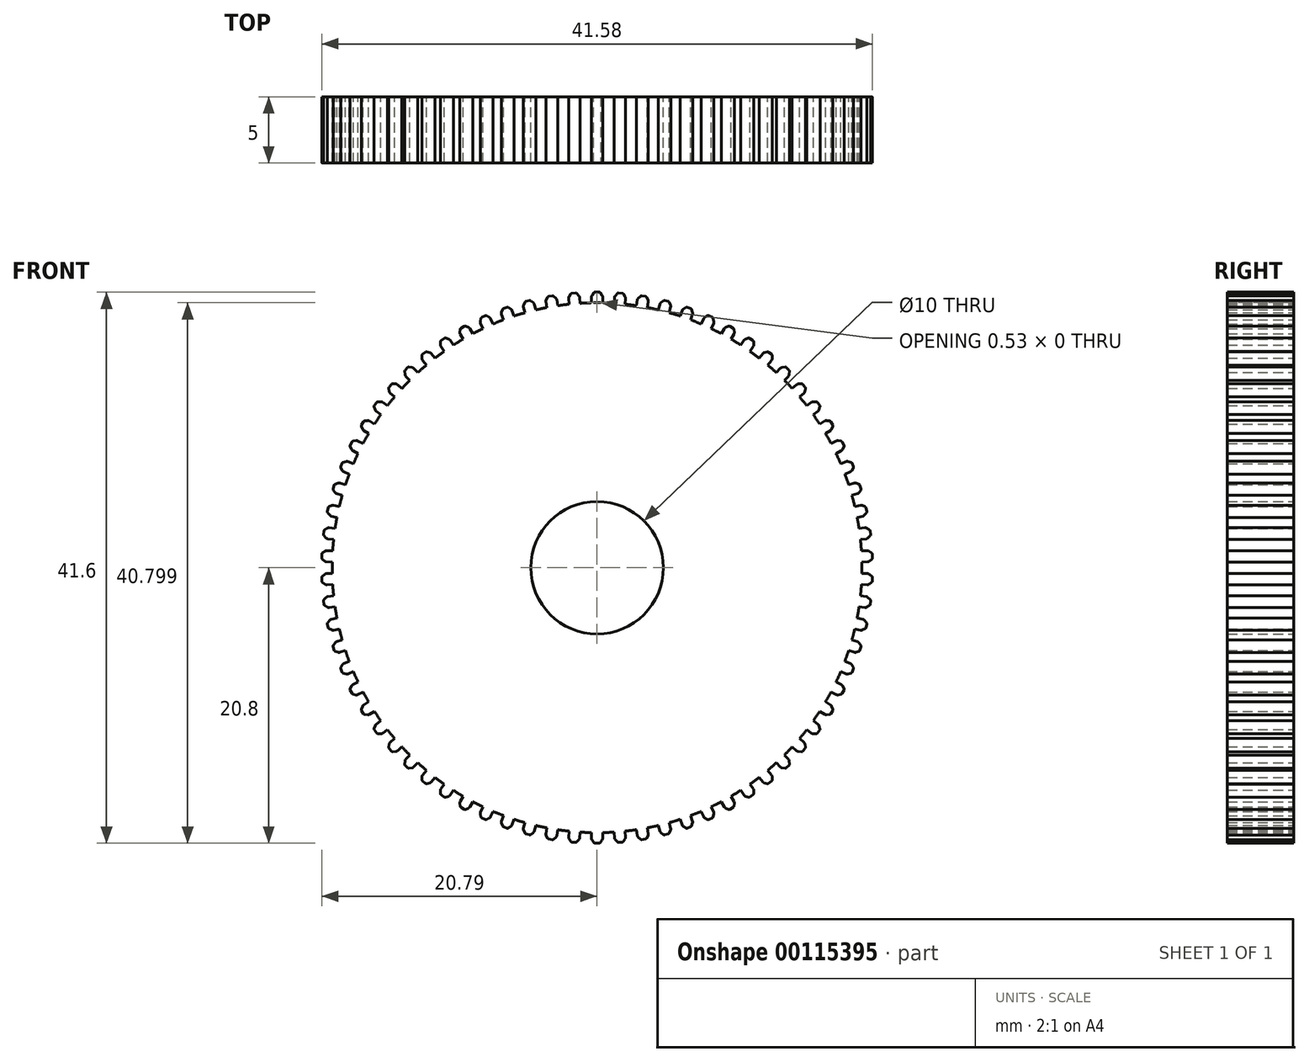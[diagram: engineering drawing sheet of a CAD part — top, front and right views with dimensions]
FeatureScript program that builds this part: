
annotation { "Feature Type Name" : "Feature", "Feature Type Description" : "" }
export const myFeature = defineFeature(function(context is Context, id is Id, definition is map)
    precondition{}
    {
        {
            var Q0;
            Q0=qCreatedBy(makeId("Front.planeOp"),FACE);
            var sketch = newSketch(context, id + "F0", { "sketchPlane" : qUnion([Q0])});
            skCircle(sketch, "E0", {"center": v(0, 0) * mm, "radius": 20 * mm});
            skLineSegment(sketch, "E1.bottom", {"start": v(0, 20.8) * mm, "end": v(-0.15, 20.8) * mm});
            skLineSegment(sketch, "E1.left", {"start": v(0, 20.8) * mm, "end": v(0, 20) * mm});
            skLineSegment(sketch, "E2.right", {"start": v(-0.42, 20.44) * mm, "end": v(-0.42, 20) * mm});
            skLineSegment(sketch, "E3", {"start": v(-0.38, 20.57) * mm, "end": v(-0.23, 20.76) * mm});
            skPoint(sketch, "E4.visualSharp", {"position": v(-0.2, 20.8) * mm});
            skArc(sketch, "E4.filletArc", {"start": v(-0.15, 20.8) * mm, "mid": v(-0.2, 20.8) * mm, "end": v(-0.23, 20.76) * mm});
            skPoint(sketch, "E5.visualSharp", {"position": v(-0.42, 20.51) * mm});
            skArc(sketch, "E5.filletArc", {"start": v(-0.38, 20.57) * mm, "mid": v(-0.4, 20.5) * mm, "end": v(-0.42, 20.44) * mm});
            skLineSegment(sketch, "E6.32.7", {"start": v(-8.82, -18.58) * mm, "end": v(-8.76, -18.82) * mm});
            skLineSegment(sketch, "E6.32.8", {"start": v(-8.13, -18.9) * mm, "end": v(-8.34, -19.01) * mm});
            skLineSegment(sketch, "E6.32.9", {"start": v(-8.57, -18.95) * mm, "end": v(-8.7, -18.9) * mm});
            skArc(sketch, "E6.32.10", {"start": v(-8.82, -18.58) * mm, "mid": v(-8.82, -18.52) * mm, "end": v(-8.8, -18.46) * mm});
            skArc(sketch, "E6.32.11", {"start": v(-8.7, -18.9) * mm, "mid": v(-8.74, -18.86) * mm, "end": v(-8.76, -18.82) * mm});
            skArc(sketch, "E6.32.12", {"start": v(-8.13, -18.9) * mm, "mid": v(-8.08, -18.86) * mm, "end": v(-8.04, -18.8) * mm});
            skArc(sketch, "E6.32.13", {"start": v(-8.43, -19.02) * mm, "mid": v(-8.39, -19.02) * mm, "end": v(-8.34, -19.01) * mm});
            skLineSegment(sketch, "E6.32.14", {"start": v(-8.57, -18.95) * mm, "end": v(-8.43, -19.02) * mm});
            skLineSegment(sketch, "E6.33.0", {"start": v(-7.21, -19.14) * mm, "end": v(-7.06, -18.71) * mm});
            skPoint(sketch, "E6.33.1", {"position": v(-6.74, -19.68) * mm});
            skLineSegment(sketch, "E6.33.2", {"start": v(-6.42, -19.42) * mm, "end": v(-6.27, -19) * mm});
            skLineSegment(sketch, "E6.33.3", {"start": v(-6.93, -19.61) * mm, "end": v(-6.66, -18.86) * mm});
            skPoint(sketch, "E6.33.6", {"position": v(-7.12, -19.55) * mm});
            skLineSegment(sketch, "E6.33.7", {"start": v(-7.2, -19.27) * mm, "end": v(-7.13, -19.5) * mm});
            skLineSegment(sketch, "E6.33.8", {"start": v(-6.5, -19.52) * mm, "end": v(-6.7, -19.65) * mm});
            skLineSegment(sketch, "E6.33.9", {"start": v(-6.93, -19.61) * mm, "end": v(-7.07, -19.56) * mm});
            skArc(sketch, "E6.33.10", {"start": v(-7.2, -19.27) * mm, "mid": v(-7.22, -19.2) * mm, "end": v(-7.2, -19.14) * mm});
            skArc(sketch, "E6.33.11", {"start": v(-7.07, -19.56) * mm, "mid": v(-7.1, -19.54) * mm, "end": v(-7.13, -19.5) * mm});
            skArc(sketch, "E6.33.12", {"start": v(-6.5, -19.52) * mm, "mid": v(-6.45, -19.47) * mm, "end": v(-6.42, -19.42) * mm});
            skArc(sketch, "E6.33.13", {"start": v(-6.79, -19.66) * mm, "mid": v(-6.74, -19.67) * mm, "end": v(-6.7, -19.65) * mm});
            skLineSegment(sketch, "E6.33.14", {"start": v(-6.93, -19.61) * mm, "end": v(-6.79, -19.66) * mm});
            skLineSegment(sketch, "E6.34.0", {"start": v(-5.56, -19.69) * mm, "end": v(-5.45, -19.24) * mm});
            skPoint(sketch, "E6.34.1", {"position": v(-5.05, -20.18) * mm});
            skLineSegment(sketch, "E6.34.2", {"start": v(-4.75, -19.9) * mm, "end": v(-4.63, -19.46) * mm});
            skLineSegment(sketch, "E6.34.3", {"start": v(-5.24, -20.13) * mm, "end": v(-5.04, -19.36) * mm});
            skPoint(sketch, "E6.34.4", {"position": v(-4.76, -19.96) * mm});
            skPoint(sketch, "E6.34.5", {"position": v(-5.58, -19.74) * mm});
            skPoint(sketch, "E6.34.6", {"position": v(-5.44, -20.08) * mm});
            skLineSegment(sketch, "E6.34.7", {"start": v(-5.55, -19.8) * mm, "end": v(-5.45, -20.03) * mm});
            skLineSegment(sketch, "E6.34.8", {"start": v(-4.82, -20) * mm, "end": v(-5.01, -20.15) * mm});
            skLineSegment(sketch, "E6.34.9", {"start": v(-5.24, -20.13) * mm, "end": v(-5.39, -20.1) * mm});
            skArc(sketch, "E6.34.10", {"start": v(-5.55, -19.8) * mm, "mid": v(-5.56, -19.74) * mm, "end": v(-5.56, -19.68) * mm});
            skArc(sketch, "E6.34.11", {"start": v(-5.39, -20.1) * mm, "mid": v(-5.43, -20.07) * mm, "end": v(-5.45, -20.03) * mm});
            skArc(sketch, "E6.34.12", {"start": v(-4.82, -20) * mm, "mid": v(-4.77, -19.95) * mm, "end": v(-4.75, -19.9) * mm});
            skArc(sketch, "E6.34.13", {"start": v(-5.1, -20.17) * mm, "mid": v(-5.05, -20.17) * mm, "end": v(-5.01, -20.15) * mm});
            skLineSegment(sketch, "E6.34.14", {"start": v(-5.24, -20.13) * mm, "end": v(-5.1, -20.17) * mm});
            skLineSegment(sketch, "E6.35.0", {"start": v(-3.87, -20.09) * mm, "end": v(-3.8, -19.64) * mm});
            skPoint(sketch, "E6.35.1", {"position": v(-3.32, -20.53) * mm});
            skLineSegment(sketch, "E6.35.2", {"start": v(-3.04, -20.22) * mm, "end": v(-2.97, -19.78) * mm});
            skLineSegment(sketch, "E6.35.3", {"start": v(-3.52, -20.5) * mm, "end": v(-3.38, -19.71) * mm});
            skPoint(sketch, "E6.35.4", {"position": v(-3.05, -20.29) * mm});
            skPoint(sketch, "E6.35.5", {"position": v(-3.88, -20.15) * mm});
            skPoint(sketch, "E6.35.6", {"position": v(-3.71, -20.47) * mm});
            skLineSegment(sketch, "E6.35.7", {"start": v(-3.85, -20.2) * mm, "end": v(-3.73, -20.42) * mm});
            skLineSegment(sketch, "E6.35.8", {"start": v(-3.1, -20.33) * mm, "end": v(-3.28, -20.5) * mm});
            skLineSegment(sketch, "E6.35.9", {"start": v(-3.52, -20.5) * mm, "end": v(-3.66, -20.48) * mm});
            skArc(sketch, "E6.35.10", {"start": v(-3.85, -20.2) * mm, "mid": v(-3.87, -20.14) * mm, "end": v(-3.87, -20.08) * mm});
            skArc(sketch, "E6.35.11", {"start": v(-3.66, -20.48) * mm, "mid": v(-3.7, -20.46) * mm, "end": v(-3.73, -20.42) * mm});
            skArc(sketch, "E6.35.12", {"start": v(-3.1, -20.33) * mm, "mid": v(-3.06, -20.28) * mm, "end": v(-3.04, -20.22) * mm});
            skArc(sketch, "E6.35.13", {"start": v(-3.37, -20.53) * mm, "mid": v(-3.32, -20.52) * mm, "end": v(-3.28, -20.5) * mm});
            skLineSegment(sketch, "E6.35.14", {"start": v(-3.52, -20.5) * mm, "end": v(-3.37, -20.53) * mm});
            skLineSegment(sketch, "E6.36.0", {"start": v(-2.15, -20.34) * mm, "end": v(-2.12, -19.89) * mm});
            skPoint(sketch, "E6.36.1", {"position": v(-1.57, -20.74) * mm});
            skLineSegment(sketch, "E6.36.2", {"start": v(-1.32, -20.4) * mm, "end": v(-1.28, -19.96) * mm});
            skLineSegment(sketch, "E6.36.3", {"start": v(-1.76, -20.73) * mm, "end": v(-1.7, -19.93) * mm});
            skPoint(sketch, "E6.36.4", {"position": v(-1.32, -20.47) * mm});
            skPoint(sketch, "E6.36.5", {"position": v(-2.16, -20.4) * mm});
            skPoint(sketch, "E6.36.6", {"position": v(-1.96, -20.7) * mm});
            skLineSegment(sketch, "E6.36.7", {"start": v(-2.12, -20.46) * mm, "end": v(-1.99, -20.67) * mm});
            skLineSegment(sketch, "E6.36.8", {"start": v(-1.37, -20.52) * mm, "end": v(-1.53, -20.7) * mm});
            skLineSegment(sketch, "E6.36.9", {"start": v(-1.76, -20.73) * mm, "end": v(-1.91, -20.71) * mm});
            skArc(sketch, "E6.36.10", {"start": v(-2.12, -20.46) * mm, "mid": v(-2.15, -20.4) * mm, "end": v(-2.15, -20.34) * mm});
            skArc(sketch, "E6.36.11", {"start": v(-1.91, -20.71) * mm, "mid": v(-1.96, -20.7) * mm, "end": v(-1.99, -20.67) * mm});
            skArc(sketch, "E6.36.12", {"start": v(-1.37, -20.52) * mm, "mid": v(-1.33, -20.47) * mm, "end": v(-1.32, -20.4) * mm});
            skArc(sketch, "E6.36.13", {"start": v(-1.62, -20.74) * mm, "mid": v(-1.57, -20.73) * mm, "end": v(-1.53, -20.7) * mm});
            skLineSegment(sketch, "E6.36.14", {"start": v(-1.76, -20.73) * mm, "end": v(-1.62, -20.74) * mm});
            skLineSegment(sketch, "E6.37.0", {"start": v(-0.42, -20.45) * mm, "end": v(-0.42, -20) * mm});
            skPoint(sketch, "E6.37.1", {"position": v(0.2, -20.8) * mm});
            skLineSegment(sketch, "E6.37.2", {"start": v(0.42, -20.44) * mm, "end": v(0.42, -20) * mm});
            skLineSegment(sketch, "E6.37.3", {"start": v(0, -20.8) * mm, "end": v(0, -20) * mm});
            skPoint(sketch, "E6.37.4", {"position": v(0.42, -20.51) * mm});
            skPoint(sketch, "E6.37.5", {"position": v(-0.42, -20.51) * mm});
            skPoint(sketch, "E6.37.6", {"position": v(-0.2, -20.8) * mm});
            skLineSegment(sketch, "E6.37.7", {"start": v(-0.38, -20.57) * mm, "end": v(-0.23, -20.76) * mm});
            skLineSegment(sketch, "E6.37.8", {"start": v(0.38, -20.57) * mm, "end": v(0.23, -20.76) * mm});
            skLineSegment(sketch, "E6.37.9", {"start": v(0, -20.8) * mm, "end": v(-0.15, -20.8) * mm});
            skArc(sketch, "E6.37.10", {"start": v(-0.38, -20.57) * mm, "mid": v(-0.4, -20.5) * mm, "end": v(-0.42, -20.44) * mm});
            skArc(sketch, "E6.37.11", {"start": v(-0.15, -20.8) * mm, "mid": v(-0.2, -20.8) * mm, "end": v(-0.23, -20.76) * mm});
            skArc(sketch, "E6.37.12", {"start": v(0.38, -20.57) * mm, "mid": v(0.4, -20.5) * mm, "end": v(0.42, -20.44) * mm});
            skArc(sketch, "E6.37.13", {"start": v(0.15, -20.8) * mm, "mid": v(0.2, -20.8) * mm, "end": v(0.23, -20.76) * mm});
            skLineSegment(sketch, "E6.37.14", {"start": v(0, -20.8) * mm, "end": v(0.15, -20.8) * mm});
            skLineSegment(sketch, "E6.38.0", {"start": v(1.31, -20.41) * mm, "end": v(1.28, -19.96) * mm});
            skPoint(sketch, "E6.38.1", {"position": v(1.96, -20.7) * mm});
            skLineSegment(sketch, "E6.38.2", {"start": v(2.15, -20.34) * mm, "end": v(2.11, -19.89) * mm});
            skLineSegment(sketch, "E6.38.3", {"start": v(1.76, -20.73) * mm, "end": v(1.7, -19.93) * mm});
            skPoint(sketch, "E6.38.4", {"position": v(2.16, -20.4) * mm});
            skPoint(sketch, "E6.38.5", {"position": v(1.32, -20.47) * mm});
            skPoint(sketch, "E6.38.6", {"position": v(1.56, -20.74) * mm});
            skLineSegment(sketch, "E6.38.7", {"start": v(1.37, -20.52) * mm, "end": v(1.53, -20.7) * mm});
            skLineSegment(sketch, "E6.38.8", {"start": v(2.12, -20.46) * mm, "end": v(1.99, -20.67) * mm});
            skLineSegment(sketch, "E6.38.9", {"start": v(1.76, -20.73) * mm, "end": v(1.61, -20.74) * mm});
            skArc(sketch, "E6.38.10", {"start": v(1.37, -20.52) * mm, "mid": v(1.33, -20.47) * mm, "end": v(1.31, -20.4) * mm});
            skArc(sketch, "E6.38.11", {"start": v(1.61, -20.74) * mm, "mid": v(1.57, -20.73) * mm, "end": v(1.53, -20.7) * mm});
            skArc(sketch, "E6.38.12", {"start": v(2.12, -20.46) * mm, "mid": v(2.15, -20.4) * mm, "end": v(2.15, -20.34) * mm});
            skArc(sketch, "E6.38.13", {"start": v(1.91, -20.71) * mm, "mid": v(1.96, -20.7) * mm, "end": v(1.99, -20.67) * mm});
            skLineSegment(sketch, "E6.38.14", {"start": v(1.76, -20.73) * mm, "end": v(1.91, -20.71) * mm});
            skLineSegment(sketch, "E6.39.0", {"start": v(3.04, -20.23) * mm, "end": v(2.96, -19.78) * mm});
            skPoint(sketch, "E6.39.1", {"position": v(3.71, -20.47) * mm});
            skLineSegment(sketch, "E6.39.2", {"start": v(3.87, -20.08) * mm, "end": v(3.8, -19.64) * mm});
            skLineSegment(sketch, "E6.39.3", {"start": v(3.51, -20.5) * mm, "end": v(3.38, -19.71) * mm});
            skPoint(sketch, "E6.39.4", {"position": v(3.88, -20.15) * mm});
            skPoint(sketch, "E6.39.5", {"position": v(3.05, -20.29) * mm});
            skPoint(sketch, "E6.39.6", {"position": v(3.32, -20.54) * mm});
            skLineSegment(sketch, "E6.39.7", {"start": v(3.1, -20.33) * mm, "end": v(3.28, -20.5) * mm});
            skLineSegment(sketch, "E6.39.8", {"start": v(3.85, -20.2) * mm, "end": v(3.73, -20.42) * mm});
            skLineSegment(sketch, "E6.39.9", {"start": v(3.52, -20.5) * mm, "end": v(3.37, -20.53) * mm});
            skArc(sketch, "E6.39.10", {"start": v(3.1, -20.33) * mm, "mid": v(3.06, -20.28) * mm, "end": v(3.04, -20.22) * mm});
            skArc(sketch, "E6.39.11", {"start": v(3.37, -20.53) * mm, "mid": v(3.32, -20.52) * mm, "end": v(3.28, -20.5) * mm});
            skArc(sketch, "E6.39.12", {"start": v(3.85, -20.2) * mm, "mid": v(3.87, -20.14) * mm, "end": v(3.87, -20.08) * mm});
            skArc(sketch, "E6.39.13", {"start": v(3.66, -20.48) * mm, "mid": v(3.7, -20.46) * mm, "end": v(3.73, -20.42) * mm});
            skLineSegment(sketch, "E6.39.14", {"start": v(3.51, -20.5) * mm, "end": v(3.66, -20.48) * mm});
            skLineSegment(sketch, "E6.40.0", {"start": v(4.75, -19.9) * mm, "end": v(4.63, -19.46) * mm});
            skPoint(sketch, "E6.40.1", {"position": v(5.43, -20.08) * mm});
            skLineSegment(sketch, "E6.40.2", {"start": v(5.56, -19.68) * mm, "end": v(5.44, -19.24) * mm});
            skLineSegment(sketch, "E6.40.3", {"start": v(5.24, -20.13) * mm, "end": v(5.04, -19.36) * mm});
            skPoint(sketch, "E6.40.4", {"position": v(5.57, -19.75) * mm});
            skPoint(sketch, "E6.40.5", {"position": v(4.76, -19.96) * mm});
            skPoint(sketch, "E6.40.6", {"position": v(5.05, -20.18) * mm});
            skLineSegment(sketch, "E6.40.7", {"start": v(4.82, -20) * mm, "end": v(5, -20.15) * mm});
            skLineSegment(sketch, "E6.40.8", {"start": v(5.55, -19.8) * mm, "end": v(5.45, -20.03) * mm});
            skLineSegment(sketch, "E6.40.9", {"start": v(5.24, -20.13) * mm, "end": v(5.1, -20.17) * mm});
            skArc(sketch, "E6.40.10", {"start": v(4.82, -20) * mm, "mid": v(4.77, -19.95) * mm, "end": v(4.74, -19.9) * mm});
            skArc(sketch, "E6.40.11", {"start": v(5.1, -20.17) * mm, "mid": v(5.05, -20.17) * mm, "end": v(5, -20.15) * mm});
            skArc(sketch, "E6.40.12", {"start": v(5.55, -19.8) * mm, "mid": v(5.56, -19.74) * mm, "end": v(5.56, -19.68) * mm});
            skArc(sketch, "E6.40.13", {"start": v(5.39, -20.1) * mm, "mid": v(5.43, -20.07) * mm, "end": v(5.45, -20.03) * mm});
            skLineSegment(sketch, "E6.40.14", {"start": v(5.24, -20.13) * mm, "end": v(5.39, -20.1) * mm});
            skLineSegment(sketch, "E6.41.0", {"start": v(6.42, -19.42) * mm, "end": v(6.26, -19) * mm});
            skPoint(sketch, "E6.41.1", {"position": v(7.12, -19.55) * mm});
            skLineSegment(sketch, "E6.41.2", {"start": v(7.2, -19.14) * mm, "end": v(7.06, -18.71) * mm});
            skLineSegment(sketch, "E6.41.3", {"start": v(6.93, -19.61) * mm, "end": v(6.66, -18.86) * mm});
            skPoint(sketch, "E6.41.6", {"position": v(6.74, -19.68) * mm});
            skLineSegment(sketch, "E6.41.7", {"start": v(6.5, -19.52) * mm, "end": v(6.7, -19.65) * mm});
            skLineSegment(sketch, "E6.41.8", {"start": v(7.2, -19.27) * mm, "end": v(7.13, -19.5) * mm});
            skLineSegment(sketch, "E6.41.9", {"start": v(6.93, -19.61) * mm, "end": v(6.79, -19.66) * mm});
            skArc(sketch, "E6.41.10", {"start": v(6.5, -19.52) * mm, "mid": v(6.45, -19.47) * mm, "end": v(6.41, -19.42) * mm});
            skArc(sketch, "E6.41.11", {"start": v(6.79, -19.66) * mm, "mid": v(6.74, -19.67) * mm, "end": v(6.7, -19.65) * mm});
            skArc(sketch, "E6.41.12", {"start": v(7.2, -19.27) * mm, "mid": v(7.22, -19.2) * mm, "end": v(7.2, -19.14) * mm});
            skArc(sketch, "E6.41.13", {"start": v(7.07, -19.56) * mm, "mid": v(7.1, -19.54) * mm, "end": v(7.13, -19.5) * mm});
            skLineSegment(sketch, "E6.41.14", {"start": v(6.93, -19.61) * mm, "end": v(7.07, -19.56) * mm});
            skLineSegment(sketch, "E6.42.7", {"start": v(8.13, -18.9) * mm, "end": v(8.34, -19.01) * mm});
            skLineSegment(sketch, "E6.42.8", {"start": v(8.82, -18.58) * mm, "end": v(8.76, -18.82) * mm});
            skLineSegment(sketch, "E6.42.9", {"start": v(8.57, -18.95) * mm, "end": v(8.43, -19.02) * mm});
            skArc(sketch, "E6.42.10", {"start": v(8.13, -18.9) * mm, "mid": v(8.07, -18.86) * mm, "end": v(8.04, -18.8) * mm});
            skArc(sketch, "E6.42.11", {"start": v(8.43, -19.02) * mm, "mid": v(8.39, -19.02) * mm, "end": v(8.34, -19.01) * mm});
            skArc(sketch, "E6.42.12", {"start": v(8.82, -18.58) * mm, "mid": v(8.82, -18.52) * mm, "end": v(8.8, -18.46) * mm});
            skArc(sketch, "E6.42.13", {"start": v(8.7, -18.9) * mm, "mid": v(8.74, -18.87) * mm, "end": v(8.76, -18.82) * mm});
            skLineSegment(sketch, "E6.42.14", {"start": v(8.57, -18.95) * mm, "end": v(8.7, -18.9) * mm});
            skCircle(sketch, "E7", {"center": v(0, 0) * mm, "radius": 5 * mm});
            skFitSpline(sketch, "E8", {"points": [v(-0.42, 20) * mm, v(0, 20) * mm, v(0.42, 20) * mm], "startDerivative": vector(0.84, 0.02) * mm, "endDerivative": vector(0.84, -0.02) * mm});
            skArc(sketch, "E9.MirrorCS", {"start": v(0.15, 20.8) * mm, "mid": v(0.2, 20.8) * mm, "end": v(0.23, 20.76) * mm});
            skArc(sketch, "E10.MirrorCS", {"start": v(0.38, 20.57) * mm, "mid": v(0.4, 20.5) * mm, "end": v(0.42, 20.44) * mm});
            skPoint(sketch, "E11.MirrorP", {"position": v(0.42, 20.51) * mm});
            skLineSegment(sketch, "E12.MirrorCS", {"start": v(0, 20.8) * mm, "end": v(0.15, 20.8) * mm});
            skLineSegment(sketch, "E13.MirrorCS", {"start": v(0.38, 20.57) * mm, "end": v(0.23, 20.76) * mm});
            skPoint(sketch, "E14.MirrorP", {"position": v(0.2, 20.8) * mm});
            skLineSegment(sketch, "E15.MirrorCS", {"start": v(0.42, 20.44) * mm, "end": v(0.42, 20) * mm});
            skPoint(sketch, "E16.1.0", {"position": v(-2.16, 20.4) * mm});
            skLineSegment(sketch, "E16.1.1", {"start": v(-1.37, 20.52) * mm, "end": v(-1.53, 20.7) * mm});
            skPoint(sketch, "E16.1.2", {"position": v(-1.32, 20.47) * mm});
            skLineSegment(sketch, "E16.1.3", {"start": v(-1.76, 20.73) * mm, "end": v(-1.7, 19.93) * mm});
            skLineSegment(sketch, "E16.1.4", {"start": v(-2.15, 20.34) * mm, "end": v(-2.11, 19.89) * mm});
            skPoint(sketch, "E16.1.5", {"position": v(-1.57, 20.74) * mm});
            skLineSegment(sketch, "E16.1.6", {"start": v(-1.76, 20.73) * mm, "end": v(-1.62, 20.74) * mm});
            skPoint(sketch, "E16.1.7", {"position": v(-1.96, 20.7) * mm});
            skLineSegment(sketch, "E16.1.8", {"start": v(-2.12, 20.46) * mm, "end": v(-1.99, 20.67) * mm});
            skLineSegment(sketch, "E16.1.9", {"start": v(-1.32, 20.4) * mm, "end": v(-1.28, 19.96) * mm});
            skArc(sketch, "E16.1.10", {"start": v(-1.91, 20.71) * mm, "mid": v(-1.96, 20.7) * mm, "end": v(-1.99, 20.67) * mm});
            skArc(sketch, "E16.1.11", {"start": v(-2.12, 20.46) * mm, "mid": v(-2.15, 20.4) * mm, "end": v(-2.15, 20.34) * mm});
            skArc(sketch, "E16.1.12", {"start": v(-1.62, 20.74) * mm, "mid": v(-1.57, 20.73) * mm, "end": v(-1.53, 20.7) * mm});
            skArc(sketch, "E16.1.13", {"start": v(-1.37, 20.52) * mm, "mid": v(-1.33, 20.47) * mm, "end": v(-1.32, 20.4) * mm});
            skLineSegment(sketch, "E16.1.14", {"start": v(-1.76, 20.73) * mm, "end": v(-1.91, 20.71) * mm});
            skPoint(sketch, "E16.2.0", {"position": v(-3.88, 20.15) * mm});
            skLineSegment(sketch, "E16.2.1", {"start": v(-3.1, 20.33) * mm, "end": v(-3.28, 20.5) * mm});
            skPoint(sketch, "E16.2.2", {"position": v(-3.05, 20.29) * mm});
            skLineSegment(sketch, "E16.2.3", {"start": v(-3.52, 20.5) * mm, "end": v(-3.38, 19.71) * mm});
            skLineSegment(sketch, "E16.2.4", {"start": v(-3.87, 20.08) * mm, "end": v(-3.8, 19.64) * mm});
            skPoint(sketch, "E16.2.5", {"position": v(-3.32, 20.53) * mm});
            skLineSegment(sketch, "E16.2.6", {"start": v(-3.52, 20.5) * mm, "end": v(-3.37, 20.53) * mm});
            skPoint(sketch, "E16.2.7", {"position": v(-3.71, 20.47) * mm});
            skLineSegment(sketch, "E16.2.8", {"start": v(-3.85, 20.2) * mm, "end": v(-3.73, 20.42) * mm});
            skLineSegment(sketch, "E16.2.9", {"start": v(-3.04, 20.22) * mm, "end": v(-2.97, 19.78) * mm});
            skArc(sketch, "E16.2.10", {"start": v(-3.66, 20.48) * mm, "mid": v(-3.7, 20.46) * mm, "end": v(-3.73, 20.42) * mm});
            skArc(sketch, "E16.2.11", {"start": v(-3.85, 20.2) * mm, "mid": v(-3.87, 20.14) * mm, "end": v(-3.87, 20.08) * mm});
            skArc(sketch, "E16.2.12", {"start": v(-3.37, 20.53) * mm, "mid": v(-3.32, 20.52) * mm, "end": v(-3.28, 20.5) * mm});
            skArc(sketch, "E16.2.13", {"start": v(-3.1, 20.33) * mm, "mid": v(-3.06, 20.28) * mm, "end": v(-3.04, 20.22) * mm});
            skLineSegment(sketch, "E16.2.14", {"start": v(-3.52, 20.5) * mm, "end": v(-3.66, 20.48) * mm});
            skPoint(sketch, "E16.3.0", {"position": v(-5.57, 19.75) * mm});
            skLineSegment(sketch, "E16.3.1", {"start": v(-4.82, 20) * mm, "end": v(-5.01, 20.15) * mm});
            skPoint(sketch, "E16.3.2", {"position": v(-4.76, 19.96) * mm});
            skLineSegment(sketch, "E16.3.3", {"start": v(-5.24, 20.13) * mm, "end": v(-5.04, 19.36) * mm});
            skLineSegment(sketch, "E16.3.4", {"start": v(-5.56, 19.68) * mm, "end": v(-5.44, 19.24) * mm});
            skPoint(sketch, "E16.3.5", {"position": v(-5.05, 20.18) * mm});
            skLineSegment(sketch, "E16.3.6", {"start": v(-5.24, 20.13) * mm, "end": v(-5.1, 20.17) * mm});
            skPoint(sketch, "E16.3.7", {"position": v(-5.43, 20.08) * mm});
            skLineSegment(sketch, "E16.3.8", {"start": v(-5.55, 19.8) * mm, "end": v(-5.45, 20.03) * mm});
            skLineSegment(sketch, "E16.3.9", {"start": v(-4.75, 19.9) * mm, "end": v(-4.63, 19.46) * mm});
            skArc(sketch, "E16.3.10", {"start": v(-5.39, 20.1) * mm, "mid": v(-5.43, 20.07) * mm, "end": v(-5.45, 20.03) * mm});
            skArc(sketch, "E16.3.11", {"start": v(-5.55, 19.8) * mm, "mid": v(-5.56, 19.74) * mm, "end": v(-5.56, 19.68) * mm});
            skArc(sketch, "E16.3.12", {"start": v(-5.1, 20.17) * mm, "mid": v(-5.05, 20.17) * mm, "end": v(-5.01, 20.15) * mm});
            skArc(sketch, "E16.3.13", {"start": v(-4.82, 20) * mm, "mid": v(-4.77, 19.95) * mm, "end": v(-4.75, 19.9) * mm});
            skLineSegment(sketch, "E16.3.14", {"start": v(-5.24, 20.13) * mm, "end": v(-5.39, 20.1) * mm});
            skPoint(sketch, "E16.4.0", {"position": v(-7.23, 19.2) * mm});
            skLineSegment(sketch, "E16.4.1", {"start": v(-6.5, 19.52) * mm, "end": v(-6.7, 19.65) * mm});
            skPoint(sketch, "E16.4.2", {"position": v(-6.44, 19.48) * mm});
            skLineSegment(sketch, "E16.4.3", {"start": v(-6.93, 19.61) * mm, "end": v(-6.66, 18.86) * mm});
            skLineSegment(sketch, "E16.4.4", {"start": v(-7.2, 19.14) * mm, "end": v(-7.06, 18.71) * mm});
            skPoint(sketch, "E16.4.5", {"position": v(-6.74, 19.68) * mm});
            skLineSegment(sketch, "E16.4.6", {"start": v(-6.93, 19.61) * mm, "end": v(-6.79, 19.66) * mm});
            skPoint(sketch, "E16.4.7", {"position": v(-7.12, 19.55) * mm});
            skLineSegment(sketch, "E16.4.8", {"start": v(-7.2, 19.27) * mm, "end": v(-7.13, 19.5) * mm});
            skLineSegment(sketch, "E16.4.9", {"start": v(-6.42, 19.42) * mm, "end": v(-6.27, 19) * mm});
            skArc(sketch, "E16.4.10", {"start": v(-7.07, 19.56) * mm, "mid": v(-7.1, 19.54) * mm, "end": v(-7.13, 19.5) * mm});
            skArc(sketch, "E16.4.11", {"start": v(-7.2, 19.27) * mm, "mid": v(-7.22, 19.2) * mm, "end": v(-7.2, 19.14) * mm});
            skArc(sketch, "E16.4.12", {"start": v(-6.79, 19.66) * mm, "mid": v(-6.74, 19.67) * mm, "end": v(-6.7, 19.65) * mm});
            skArc(sketch, "E16.4.13", {"start": v(-6.5, 19.52) * mm, "mid": v(-6.45, 19.47) * mm, "end": v(-6.42, 19.42) * mm});
            skLineSegment(sketch, "E16.4.14", {"start": v(-6.93, 19.61) * mm, "end": v(-7.07, 19.56) * mm});
            skPoint(sketch, "E16.5.0", {"position": v(-8.83, 18.52) * mm});
            skLineSegment(sketch, "E16.5.1", {"start": v(-8.13, 18.9) * mm, "end": v(-8.34, 19.01) * mm});
            skPoint(sketch, "E16.5.2", {"position": v(-8.07, 18.86) * mm});
            skLineSegment(sketch, "E16.5.3", {"start": v(-8.57, 18.95) * mm, "end": v(-8.24, 18.23) * mm});
            skLineSegment(sketch, "E16.5.4", {"start": v(-8.8, 18.46) * mm, "end": v(-8.62, 18.05) * mm});
            skPoint(sketch, "E16.5.5", {"position": v(-8.39, 19.04) * mm});
            skLineSegment(sketch, "E16.5.6", {"start": v(-8.57, 18.95) * mm, "end": v(-8.43, 19.02) * mm});
            skPoint(sketch, "E16.5.7", {"position": v(-8.75, 18.87) * mm});
            skLineSegment(sketch, "E16.5.8", {"start": v(-8.82, 18.58) * mm, "end": v(-8.76, 18.82) * mm});
            skLineSegment(sketch, "E16.5.9", {"start": v(-8.04, 18.8) * mm, "end": v(-7.85, 18.4) * mm});
            skArc(sketch, "E16.5.10", {"start": v(-8.7, 18.9) * mm, "mid": v(-8.74, 18.87) * mm, "end": v(-8.76, 18.82) * mm});
            skArc(sketch, "E16.5.11", {"start": v(-8.82, 18.58) * mm, "mid": v(-8.82, 18.52) * mm, "end": v(-8.8, 18.46) * mm});
            skArc(sketch, "E16.5.12", {"start": v(-8.43, 19.02) * mm, "mid": v(-8.39, 19.02) * mm, "end": v(-8.34, 19.01) * mm});
            skArc(sketch, "E16.5.13", {"start": v(-8.13, 18.9) * mm, "mid": v(-8.08, 18.86) * mm, "end": v(-8.04, 18.8) * mm});
            skLineSegment(sketch, "E16.5.14", {"start": v(-8.57, 18.95) * mm, "end": v(-8.7, 18.9) * mm});
            skPoint(sketch, "E16.6.0", {"position": v(-10.37, 17.7) * mm});
            skLineSegment(sketch, "E16.6.1", {"start": v(-9.7, 18.14) * mm, "end": v(-9.93, 18.24) * mm});
            skPoint(sketch, "E16.6.2", {"position": v(-9.64, 18.11) * mm});
            skLineSegment(sketch, "E16.6.3", {"start": v(-10.14, 18.16) * mm, "end": v(-9.75, 17.46) * mm});
            skLineSegment(sketch, "E16.6.4", {"start": v(-10.34, 17.64) * mm, "end": v(-10.12, 17.25) * mm});
            skPoint(sketch, "E16.6.5", {"position": v(-9.97, 18.26) * mm});
            skLineSegment(sketch, "E16.6.6", {"start": v(-10.14, 18.16) * mm, "end": v(-10.01, 18.23) * mm});
            skPoint(sketch, "E16.6.7", {"position": v(-10.32, 18.06) * mm});
            skLineSegment(sketch, "E16.6.8", {"start": v(-10.36, 17.77) * mm, "end": v(-10.32, 18.01) * mm});
            skLineSegment(sketch, "E16.6.9", {"start": v(-9.6, 18.05) * mm, "end": v(-9.39, 17.66) * mm});
            skArc(sketch, "E16.6.10", {"start": v(-10.27, 18.09) * mm, "mid": v(-10.3, 18.06) * mm, "end": v(-10.32, 18.01) * mm});
            skArc(sketch, "E16.6.11", {"start": v(-10.36, 17.77) * mm, "mid": v(-10.36, 17.7) * mm, "end": v(-10.34, 17.64) * mm});
            skArc(sketch, "E16.6.12", {"start": v(-10.01, 18.23) * mm, "mid": v(-9.97, 18.24) * mm, "end": v(-9.93, 18.24) * mm});
            skArc(sketch, "E16.6.13", {"start": v(-9.7, 18.14) * mm, "mid": v(-9.65, 18.1) * mm, "end": v(-9.6, 18.05) * mm});
            skLineSegment(sketch, "E16.6.14", {"start": v(-10.14, 18.16) * mm, "end": v(-10.27, 18.09) * mm});
            skPoint(sketch, "E16.7.0", {"position": v(-11.83, 16.76) * mm});
            skLineSegment(sketch, "E16.7.1", {"start": v(-11.2, 17.25) * mm, "end": v(-11.44, 17.33) * mm});
            skPoint(sketch, "E16.7.2", {"position": v(-11.14, 17.23) * mm});
            skLineSegment(sketch, "E16.7.3", {"start": v(-11.65, 17.23) * mm, "end": v(-11.2, 16.57) * mm});
            skLineSegment(sketch, "E16.7.4", {"start": v(-11.8, 16.7) * mm, "end": v(-11.54, 16.33) * mm});
            skPoint(sketch, "E16.7.5", {"position": v(-11.48, 17.34) * mm});
            skLineSegment(sketch, "E16.7.6", {"start": v(-11.65, 17.23) * mm, "end": v(-11.52, 17.32) * mm});
            skPoint(sketch, "E16.7.7", {"position": v(-11.81, 17.12) * mm});
            skLineSegment(sketch, "E16.7.8", {"start": v(-11.83, 16.83) * mm, "end": v(-11.82, 17.07) * mm});
            skLineSegment(sketch, "E16.7.9", {"start": v(-11.1, 17.17) * mm, "end": v(-10.85, 16.8) * mm});
            skArc(sketch, "E16.7.10", {"start": v(-11.77, 17.15) * mm, "mid": v(-11.8, 17.12) * mm, "end": v(-11.82, 17.07) * mm});
            skArc(sketch, "E16.7.11", {"start": v(-11.83, 16.83) * mm, "mid": v(-11.82, 16.76) * mm, "end": v(-11.8, 16.7) * mm});
            skArc(sketch, "E16.7.12", {"start": v(-11.52, 17.32) * mm, "mid": v(-11.48, 17.33) * mm, "end": v(-11.44, 17.33) * mm});
            skArc(sketch, "E16.7.13", {"start": v(-11.2, 17.25) * mm, "mid": v(-11.15, 17.22) * mm, "end": v(-11.1, 17.17) * mm});
            skLineSegment(sketch, "E16.7.14", {"start": v(-11.65, 17.23) * mm, "end": v(-11.77, 17.15) * mm});
            skPoint(sketch, "E16.8.0", {"position": v(-13.21, 15.7) * mm});
            skLineSegment(sketch, "E16.8.1", {"start": v(-12.63, 16.24) * mm, "end": v(-12.87, 16.3) * mm});
            skPoint(sketch, "E16.8.2", {"position": v(-12.56, 16.22) * mm});
            skLineSegment(sketch, "E16.8.3", {"start": v(-13.07, 16.18) * mm, "end": v(-12.56, 15.56) * mm});
            skLineSegment(sketch, "E16.8.4", {"start": v(-13.17, 15.64) * mm, "end": v(-12.89, 15.3) * mm});
            skPoint(sketch, "E16.8.5", {"position": v(-12.91, 16.3) * mm});
            skLineSegment(sketch, "E16.8.6", {"start": v(-13.07, 16.18) * mm, "end": v(-12.95, 16.28) * mm});
            skPoint(sketch, "E16.8.7", {"position": v(-13.22, 16.06) * mm});
            skLineSegment(sketch, "E16.8.8", {"start": v(-13.21, 15.76) * mm, "end": v(-13.22, 16) * mm});
            skLineSegment(sketch, "E16.8.9", {"start": v(-12.52, 16.17) * mm, "end": v(-12.24, 15.82) * mm});
            skArc(sketch, "E16.8.10", {"start": v(-13.18, 16.09) * mm, "mid": v(-13.21, 16.05) * mm, "end": v(-13.22, 16) * mm});
            skArc(sketch, "E16.8.11", {"start": v(-13.21, 15.76) * mm, "mid": v(-13.2, 15.7) * mm, "end": v(-13.17, 15.64) * mm});
            skArc(sketch, "E16.8.12", {"start": v(-12.95, 16.28) * mm, "mid": v(-12.91, 16.3) * mm, "end": v(-12.87, 16.3) * mm});
            skArc(sketch, "E16.8.13", {"start": v(-12.63, 16.24) * mm, "mid": v(-12.57, 16.21) * mm, "end": v(-12.52, 16.17) * mm});
            skLineSegment(sketch, "E16.8.14", {"start": v(-13.07, 16.18) * mm, "end": v(-13.18, 16.09) * mm});
            skPoint(sketch, "E16.9.0", {"position": v(-14.5, 14.52) * mm});
            skLineSegment(sketch, "E16.9.1", {"start": v(-13.96, 15.1) * mm, "end": v(-14.2, 15.15) * mm});
            skPoint(sketch, "E16.9.2", {"position": v(-13.9, 15.1) * mm});
            skLineSegment(sketch, "E16.9.3", {"start": v(-14.4, 15.02) * mm, "end": v(-13.84, 14.44) * mm});
            skLineSegment(sketch, "E16.9.4", {"start": v(-14.45, 14.47) * mm, "end": v(-14.14, 14.15) * mm});
            skPoint(sketch, "E16.9.5", {"position": v(-14.25, 15.15) * mm});
            skLineSegment(sketch, "E16.9.6", {"start": v(-14.4, 15.02) * mm, "end": v(-14.29, 15.12) * mm});
            skPoint(sketch, "E16.9.7", {"position": v(-14.54, 14.88) * mm});
            skLineSegment(sketch, "E16.9.8", {"start": v(-14.5, 14.59) * mm, "end": v(-14.53, 14.83) * mm});
            skLineSegment(sketch, "E16.9.9", {"start": v(-13.84, 15.05) * mm, "end": v(-13.53, 14.73) * mm});
            skArc(sketch, "E16.9.10", {"start": v(-14.5, 14.91) * mm, "mid": v(-14.53, 14.88) * mm, "end": v(-14.53, 14.83) * mm});
            skArc(sketch, "E16.9.11", {"start": v(-14.5, 14.59) * mm, "mid": v(-14.49, 14.52) * mm, "end": v(-14.45, 14.47) * mm});
            skArc(sketch, "E16.9.12", {"start": v(-14.29, 15.12) * mm, "mid": v(-14.25, 15.14) * mm, "end": v(-14.2, 15.15) * mm});
            skArc(sketch, "E16.9.13", {"start": v(-13.96, 15.1) * mm, "mid": v(-13.9, 15.09) * mm, "end": v(-13.84, 15.05) * mm});
            skLineSegment(sketch, "E16.9.14", {"start": v(-14.4, 15.02) * mm, "end": v(-14.5, 14.91) * mm});
            skPoint(sketch, "E16.10.0", {"position": v(-15.68, 13.24) * mm});
            skLineSegment(sketch, "E16.10.1", {"start": v(-15.19, 13.87) * mm, "end": v(-15.43, 13.89) * mm});
            skPoint(sketch, "E16.10.2", {"position": v(-15.12, 13.87) * mm});
            skLineSegment(sketch, "E16.10.3", {"start": v(-15.61, 13.74) * mm, "end": v(-15.01, 13.21) * mm});
            skLineSegment(sketch, "E16.10.4", {"start": v(-15.62, 13.2) * mm, "end": v(-15.29, 12.9) * mm});
            skPoint(sketch, "E16.10.5", {"position": v(-15.48, 13.9) * mm});
            skLineSegment(sketch, "E16.10.6", {"start": v(-15.61, 13.74) * mm, "end": v(-15.52, 13.85) * mm});
            skPoint(sketch, "E16.10.7", {"position": v(-15.75, 13.6) * mm});
            skLineSegment(sketch, "E16.10.8", {"start": v(-15.69, 13.3) * mm, "end": v(-15.74, 13.55) * mm});
            skLineSegment(sketch, "E16.10.9", {"start": v(-15.07, 13.82) * mm, "end": v(-14.73, 13.53) * mm});
            skArc(sketch, "E16.10.10", {"start": v(-15.71, 13.63) * mm, "mid": v(-15.73, 13.6) * mm, "end": v(-15.74, 13.55) * mm});
            skArc(sketch, "E16.10.11", {"start": v(-15.69, 13.3) * mm, "mid": v(-15.67, 13.24) * mm, "end": v(-15.62, 13.2) * mm});
            skArc(sketch, "E16.10.12", {"start": v(-15.52, 13.85) * mm, "mid": v(-15.48, 13.88) * mm, "end": v(-15.43, 13.89) * mm});
            skArc(sketch, "E16.10.13", {"start": v(-15.19, 13.87) * mm, "mid": v(-15.13, 13.86) * mm, "end": v(-15.07, 13.82) * mm});
            skLineSegment(sketch, "E16.10.14", {"start": v(-15.61, 13.74) * mm, "end": v(-15.71, 13.63) * mm});
            skPoint(sketch, "E16.11.0", {"position": v(-16.74, 11.86) * mm});
            skLineSegment(sketch, "E16.11.1", {"start": v(-16.31, 12.53) * mm, "end": v(-16.56, 12.53) * mm});
            skPoint(sketch, "E16.11.2", {"position": v(-16.24, 12.53) * mm});
            skLineSegment(sketch, "E16.11.3", {"start": v(-16.72, 12.37) * mm, "end": v(-16.08, 11.9) * mm});
            skLineSegment(sketch, "E16.11.4", {"start": v(-16.69, 11.82) * mm, "end": v(-16.33, 11.55) * mm});
            skPoint(sketch, "E16.11.5", {"position": v(-16.6, 12.53) * mm});
            skLineSegment(sketch, "E16.11.6", {"start": v(-16.72, 12.37) * mm, "end": v(-16.63, 12.49) * mm});
            skPoint(sketch, "E16.11.7", {"position": v(-16.84, 12.2) * mm});
            skLineSegment(sketch, "E16.11.8", {"start": v(-16.76, 11.93) * mm, "end": v(-16.83, 12.16) * mm});
            skLineSegment(sketch, "E16.11.9", {"start": v(-16.19, 12.5) * mm, "end": v(-15.83, 12.23) * mm});
            skArc(sketch, "E16.11.10", {"start": v(-16.81, 12.25) * mm, "mid": v(-16.83, 12.2) * mm, "end": v(-16.83, 12.16) * mm});
            skArc(sketch, "E16.11.11", {"start": v(-16.76, 11.93) * mm, "mid": v(-16.73, 11.87) * mm, "end": v(-16.69, 11.82) * mm});
            skArc(sketch, "E16.11.12", {"start": v(-16.63, 12.49) * mm, "mid": v(-16.6, 12.52) * mm, "end": v(-16.56, 12.53) * mm});
            skArc(sketch, "E16.11.13", {"start": v(-16.31, 12.53) * mm, "mid": v(-16.25, 12.52) * mm, "end": v(-16.19, 12.5) * mm});
            skLineSegment(sketch, "E16.11.14", {"start": v(-16.72, 12.37) * mm, "end": v(-16.81, 12.25) * mm});
            skPoint(sketch, "E16.12.0", {"position": v(-17.69, 10.4) * mm});
            skLineSegment(sketch, "E16.12.1", {"start": v(-17.31, 11.1) * mm, "end": v(-17.56, 11.08) * mm});
            skPoint(sketch, "E16.12.2", {"position": v(-17.25, 11.11) * mm});
            skLineSegment(sketch, "E16.12.3", {"start": v(-17.71, 10.9) * mm, "end": v(-17.03, 10.49) * mm});
            skLineSegment(sketch, "E16.12.4", {"start": v(-17.63, 10.36) * mm, "end": v(-17.25, 10.13) * mm});
            skPoint(sketch, "E16.12.5", {"position": v(-17.6, 11.07) * mm});
            skLineSegment(sketch, "E16.12.6", {"start": v(-17.71, 10.9) * mm, "end": v(-17.63, 11.03) * mm});
            skPoint(sketch, "E16.12.7", {"position": v(-17.82, 10.74) * mm});
            skLineSegment(sketch, "E16.12.8", {"start": v(-17.71, 10.46) * mm, "end": v(-17.8, 10.7) * mm});
            skLineSegment(sketch, "E16.12.9", {"start": v(-17.19, 11.08) * mm, "end": v(-16.8, 10.84) * mm});
            skArc(sketch, "E16.12.10", {"start": v(-17.8, 10.78) * mm, "mid": v(-17.8, 10.74) * mm, "end": v(-17.8, 10.7) * mm});
            skArc(sketch, "E16.12.11", {"start": v(-17.71, 10.46) * mm, "mid": v(-17.68, 10.4) * mm, "end": v(-17.63, 10.36) * mm});
            skArc(sketch, "E16.12.12", {"start": v(-17.63, 11.03) * mm, "mid": v(-17.6, 11.07) * mm, "end": v(-17.56, 11.08) * mm});
            skArc(sketch, "E16.12.13", {"start": v(-17.31, 11.1) * mm, "mid": v(-17.25, 11.1) * mm, "end": v(-17.19, 11.08) * mm});
            skLineSegment(sketch, "E16.12.14", {"start": v(-17.71, 10.9) * mm, "end": v(-17.8, 10.78) * mm});
            skPoint(sketch, "E16.13.0", {"position": v(-18.5, 8.86) * mm});
            skLineSegment(sketch, "E16.13.1", {"start": v(-18.2, 9.6) * mm, "end": v(-18.44, 9.55) * mm});
            skPoint(sketch, "E16.13.2", {"position": v(-18.13, 9.6) * mm});
            skLineSegment(sketch, "E16.13.3", {"start": v(-18.57, 9.36) * mm, "end": v(-17.86, 9) * mm});
            skLineSegment(sketch, "E16.13.4", {"start": v(-18.44, 8.83) * mm, "end": v(-18.04, 8.63) * mm});
            skPoint(sketch, "E16.13.5", {"position": v(-18.48, 9.54) * mm});
            skLineSegment(sketch, "E16.13.6", {"start": v(-18.57, 9.36) * mm, "end": v(-18.5, 9.5) * mm});
            skPoint(sketch, "E16.13.7", {"position": v(-18.66, 9.19) * mm});
            skLineSegment(sketch, "E16.13.8", {"start": v(-18.53, 8.92) * mm, "end": v(-18.64, 9.14) * mm});
            skLineSegment(sketch, "E16.13.9", {"start": v(-18.07, 9.58) * mm, "end": v(-17.67, 9.38) * mm});
            skArc(sketch, "E16.13.10", {"start": v(-18.64, 9.23) * mm, "mid": v(-18.65, 9.19) * mm, "end": v(-18.64, 9.14) * mm});
            skArc(sketch, "E16.13.11", {"start": v(-18.53, 8.92) * mm, "mid": v(-18.5, 8.87) * mm, "end": v(-18.44, 8.83) * mm});
            skArc(sketch, "E16.13.12", {"start": v(-18.5, 9.5) * mm, "mid": v(-18.48, 9.53) * mm, "end": v(-18.44, 9.55) * mm});
            skArc(sketch, "E16.13.13", {"start": v(-18.2, 9.6) * mm, "mid": v(-18.13, 9.6) * mm, "end": v(-18.07, 9.58) * mm});
            skLineSegment(sketch, "E16.13.14", {"start": v(-18.57, 9.36) * mm, "end": v(-18.64, 9.23) * mm});
            skPoint(sketch, "E16.14.0", {"position": v(-19.19, 7.26) * mm});
            skLineSegment(sketch, "E16.14.1", {"start": v(-18.94, 8.02) * mm, "end": v(-19.18, 7.95) * mm});
            skPoint(sketch, "E16.14.2", {"position": v(-18.88, 8.04) * mm});
            skLineSegment(sketch, "E16.14.3", {"start": v(-19.3, 7.76) * mm, "end": v(-18.56, 7.46) * mm});
            skLineSegment(sketch, "E16.14.4", {"start": v(-19.13, 7.23) * mm, "end": v(-18.71, 7.07) * mm});
            skPoint(sketch, "E16.14.5", {"position": v(-19.23, 7.94) * mm});
            skLineSegment(sketch, "E16.14.6", {"start": v(-19.3, 7.76) * mm, "end": v(-19.25, 7.9) * mm});
            skPoint(sketch, "E16.14.7", {"position": v(-19.37, 7.57) * mm});
            skLineSegment(sketch, "E16.14.8", {"start": v(-19.22, 7.32) * mm, "end": v(-19.35, 7.53) * mm});
            skLineSegment(sketch, "E16.14.9", {"start": v(-18.81, 8.01) * mm, "end": v(-18.4, 7.84) * mm});
            skArc(sketch, "E16.14.10", {"start": v(-19.36, 7.62) * mm, "mid": v(-19.36, 7.57) * mm, "end": v(-19.35, 7.53) * mm});
            skArc(sketch, "E16.14.11", {"start": v(-19.22, 7.32) * mm, "mid": v(-19.18, 7.27) * mm, "end": v(-19.13, 7.23) * mm});
            skArc(sketch, "E16.14.12", {"start": v(-19.25, 7.9) * mm, "mid": v(-19.22, 7.93) * mm, "end": v(-19.18, 7.95) * mm});
            skArc(sketch, "E16.14.13", {"start": v(-18.94, 8.02) * mm, "mid": v(-18.88, 8.03) * mm, "end": v(-18.81, 8.01) * mm});
            skLineSegment(sketch, "E16.14.14", {"start": v(-19.3, 7.76) * mm, "end": v(-19.36, 7.62) * mm});
            skPoint(sketch, "E16.15.0", {"position": v(-19.74, 5.6) * mm});
            skLineSegment(sketch, "E16.15.1", {"start": v(-19.55, 6.38) * mm, "end": v(-19.78, 6.3) * mm});
            skPoint(sketch, "E16.15.2", {"position": v(-19.5, 6.4) * mm});
            skLineSegment(sketch, "E16.15.3", {"start": v(-19.89, 6.1) * mm, "end": v(-19.12, 5.86) * mm});
            skLineSegment(sketch, "E16.15.4", {"start": v(-19.67, 5.59) * mm, "end": v(-19.24, 5.45) * mm});
            skPoint(sketch, "E16.15.5", {"position": v(-19.83, 6.28) * mm});
            skLineSegment(sketch, "E16.15.6", {"start": v(-19.89, 6.1) * mm, "end": v(-19.85, 6.23) * mm});
            skPoint(sketch, "E16.15.7", {"position": v(-19.95, 5.9) * mm});
            skLineSegment(sketch, "E16.15.8", {"start": v(-19.78, 5.66) * mm, "end": v(-19.92, 5.86) * mm});
            skLineSegment(sketch, "E16.15.9", {"start": v(-19.43, 6.39) * mm, "end": v(-19, 6.26) * mm});
            skArc(sketch, "E16.15.10", {"start": v(-19.93, 5.95) * mm, "mid": v(-19.94, 5.9) * mm, "end": v(-19.92, 5.86) * mm});
            skArc(sketch, "E16.15.11", {"start": v(-19.78, 5.66) * mm, "mid": v(-19.73, 5.61) * mm, "end": v(-19.67, 5.59) * mm});
            skArc(sketch, "E16.15.12", {"start": v(-19.85, 6.23) * mm, "mid": v(-19.82, 6.27) * mm, "end": v(-19.78, 6.3) * mm});
            skArc(sketch, "E16.15.13", {"start": v(-19.55, 6.38) * mm, "mid": v(-19.5, 6.4) * mm, "end": v(-19.43, 6.39) * mm});
            skLineSegment(sketch, "E16.15.14", {"start": v(-19.89, 6.1) * mm, "end": v(-19.93, 5.95) * mm});
            skPoint(sketch, "E16.16.0", {"position": v(-20.14, 3.91) * mm});
            skLineSegment(sketch, "E16.16.1", {"start": v(-20.03, 4.7) * mm, "end": v(-20.25, 4.6) * mm});
            skPoint(sketch, "E16.16.2", {"position": v(-19.96, 4.73) * mm});
            skLineSegment(sketch, "E16.16.3", {"start": v(-20.33, 4.38) * mm, "end": v(-19.55, 4.21) * mm});
            skLineSegment(sketch, "E16.16.4", {"start": v(-20.07, 3.9) * mm, "end": v(-19.64, 3.8) * mm});
            skPoint(sketch, "E16.16.5", {"position": v(-20.3, 4.58) * mm});
            skLineSegment(sketch, "E16.16.6", {"start": v(-20.33, 4.38) * mm, "end": v(-20.3, 4.53) * mm});
            skPoint(sketch, "E16.16.7", {"position": v(-20.38, 4.19) * mm});
            skLineSegment(sketch, "E16.16.8", {"start": v(-20.18, 3.96) * mm, "end": v(-20.34, 4.15) * mm});
            skLineSegment(sketch, "E16.16.9", {"start": v(-19.9, 4.72) * mm, "end": v(-19.46, 4.62) * mm});
            skArc(sketch, "E16.16.10", {"start": v(-20.37, 4.24) * mm, "mid": v(-20.36, 4.2) * mm, "end": v(-20.34, 4.15) * mm});
            skArc(sketch, "E16.16.11", {"start": v(-20.18, 3.96) * mm, "mid": v(-20.13, 3.92) * mm, "end": v(-20.07, 3.9) * mm});
            skArc(sketch, "E16.16.12", {"start": v(-20.3, 4.53) * mm, "mid": v(-20.28, 4.57) * mm, "end": v(-20.25, 4.6) * mm});
            skArc(sketch, "E16.16.13", {"start": v(-20.03, 4.7) * mm, "mid": v(-19.96, 4.72) * mm, "end": v(-19.9, 4.72) * mm});
            skLineSegment(sketch, "E16.16.14", {"start": v(-20.33, 4.38) * mm, "end": v(-20.37, 4.24) * mm});
            skPoint(sketch, "E16.17.0", {"position": v(-20.4, 2.19) * mm});
            skLineSegment(sketch, "E16.17.1", {"start": v(-20.35, 2.99) * mm, "end": v(-20.56, 2.86) * mm});
            skPoint(sketch, "E16.17.2", {"position": v(-20.3, 3.02) * mm});
            skLineSegment(sketch, "E16.17.3", {"start": v(-20.63, 2.64) * mm, "end": v(-19.84, 2.54) * mm});
            skLineSegment(sketch, "E16.17.4", {"start": v(-20.33, 2.18) * mm, "end": v(-19.89, 2.12) * mm});
            skPoint(sketch, "E16.17.5", {"position": v(-20.6, 2.84) * mm});
            skLineSegment(sketch, "E16.17.6", {"start": v(-20.63, 2.64) * mm, "end": v(-20.61, 2.79) * mm});
            skPoint(sketch, "E16.17.7", {"position": v(-20.66, 2.45) * mm});
            skLineSegment(sketch, "E16.17.8", {"start": v(-20.45, 2.24) * mm, "end": v(-20.62, 2.41) * mm});
            skLineSegment(sketch, "E16.17.9", {"start": v(-20.23, 3.01) * mm, "end": v(-19.78, 2.96) * mm});
            skArc(sketch, "E16.17.10", {"start": v(-20.65, 2.5) * mm, "mid": v(-20.65, 2.45) * mm, "end": v(-20.62, 2.41) * mm});
            skArc(sketch, "E16.17.11", {"start": v(-20.45, 2.24) * mm, "mid": v(-20.4, 2.2) * mm, "end": v(-20.33, 2.18) * mm});
            skArc(sketch, "E16.17.12", {"start": v(-20.61, 2.79) * mm, "mid": v(-20.6, 2.83) * mm, "end": v(-20.56, 2.86) * mm});
            skArc(sketch, "E16.17.13", {"start": v(-20.35, 2.99) * mm, "mid": v(-20.3, 3.01) * mm, "end": v(-20.23, 3.01) * mm});
            skLineSegment(sketch, "E16.17.14", {"start": v(-20.63, 2.64) * mm, "end": v(-20.65, 2.5) * mm});
            skPoint(sketch, "E16.18.0", {"position": v(-20.51, 0.45) * mm});
            skLineSegment(sketch, "E16.18.1", {"start": v(-20.53, 1.25) * mm, "end": v(-20.73, 1.1) * mm});
            skPoint(sketch, "E16.18.2", {"position": v(-20.48, 1.29) * mm});
            skLineSegment(sketch, "E16.18.3", {"start": v(-20.78, 0.88) * mm, "end": v(-19.98, 0.85) * mm});
            skLineSegment(sketch, "E16.18.4", {"start": v(-20.44, 0.45) * mm, "end": v(-20, 0.43) * mm});
            skPoint(sketch, "E16.18.5", {"position": v(-20.77, 1.08) * mm});
            skLineSegment(sketch, "E16.18.6", {"start": v(-20.78, 0.88) * mm, "end": v(-20.78, 1.03) * mm});
            skPoint(sketch, "E16.18.7", {"position": v(-20.8, 0.68) * mm});
            skLineSegment(sketch, "E16.18.8", {"start": v(-20.56, 0.5) * mm, "end": v(-20.75, 0.65) * mm});
            skLineSegment(sketch, "E16.18.9", {"start": v(-20.4, 1.29) * mm, "end": v(-19.96, 1.27) * mm});
            skArc(sketch, "E16.18.10", {"start": v(-20.79, 0.73) * mm, "mid": v(-20.78, 0.69) * mm, "end": v(-20.75, 0.65) * mm});
            skArc(sketch, "E16.18.11", {"start": v(-20.56, 0.5) * mm, "mid": v(-20.5, 0.46) * mm, "end": v(-20.44, 0.45) * mm});
            skArc(sketch, "E16.18.12", {"start": v(-20.78, 1.03) * mm, "mid": v(-20.76, 1.08) * mm, "end": v(-20.73, 1.1) * mm});
            skArc(sketch, "E16.18.13", {"start": v(-20.53, 1.25) * mm, "mid": v(-20.47, 1.28) * mm, "end": v(-20.4, 1.29) * mm});
            skLineSegment(sketch, "E16.18.14", {"start": v(-20.78, 0.88) * mm, "end": v(-20.79, 0.73) * mm});
            skPoint(sketch, "E16.19.0", {"position": v(-20.48, -1.29) * mm});
            skLineSegment(sketch, "E16.19.1", {"start": v(-20.56, -0.5) * mm, "end": v(-20.75, -0.65) * mm});
            skPoint(sketch, "E16.19.2", {"position": v(-20.51, -0.45) * mm});
            skLineSegment(sketch, "E16.19.3", {"start": v(-20.78, -0.88) * mm, "end": v(-19.98, -0.85) * mm});
            skLineSegment(sketch, "E16.19.4", {"start": v(-20.4, -1.29) * mm, "end": v(-19.96, -1.27) * mm});
            skPoint(sketch, "E16.19.5", {"position": v(-20.8, -0.68) * mm});
            skLineSegment(sketch, "E16.19.6", {"start": v(-20.78, -0.88) * mm, "end": v(-20.79, -0.73) * mm});
            skPoint(sketch, "E16.19.7", {"position": v(-20.77, -1.08) * mm});
            skLineSegment(sketch, "E16.19.8", {"start": v(-20.53, -1.25) * mm, "end": v(-20.73, -1.1) * mm});
            skLineSegment(sketch, "E16.19.9", {"start": v(-20.44, -0.45) * mm, "end": v(-20, -0.43) * mm});
            skArc(sketch, "E16.19.10", {"start": v(-20.78, -1.03) * mm, "mid": v(-20.76, -1.08) * mm, "end": v(-20.73, -1.1) * mm});
            skArc(sketch, "E16.19.11", {"start": v(-20.53, -1.25) * mm, "mid": v(-20.47, -1.28) * mm, "end": v(-20.4, -1.29) * mm});
            skArc(sketch, "E16.19.12", {"start": v(-20.79, -0.73) * mm, "mid": v(-20.78, -0.69) * mm, "end": v(-20.75, -0.65) * mm});
            skArc(sketch, "E16.19.13", {"start": v(-20.56, -0.5) * mm, "mid": v(-20.5, -0.46) * mm, "end": v(-20.44, -0.45) * mm});
            skLineSegment(sketch, "E16.19.14", {"start": v(-20.78, -0.88) * mm, "end": v(-20.78, -1.03) * mm});
            skPoint(sketch, "E16.20.0", {"position": v(-20.3, -3.02) * mm});
            skLineSegment(sketch, "E16.20.1", {"start": v(-20.45, -2.24) * mm, "end": v(-20.62, -2.41) * mm});
            skPoint(sketch, "E16.20.2", {"position": v(-20.4, -2.19) * mm});
            skLineSegment(sketch, "E16.20.3", {"start": v(-20.63, -2.64) * mm, "end": v(-19.84, -2.54) * mm});
            skLineSegment(sketch, "E16.20.4", {"start": v(-20.23, -3.01) * mm, "end": v(-19.78, -2.96) * mm});
            skPoint(sketch, "E16.20.5", {"position": v(-20.66, -2.45) * mm});
            skLineSegment(sketch, "E16.20.6", {"start": v(-20.63, -2.64) * mm, "end": v(-20.65, -2.5) * mm});
            skPoint(sketch, "E16.20.7", {"position": v(-20.6, -2.84) * mm});
            skLineSegment(sketch, "E16.20.8", {"start": v(-20.35, -2.99) * mm, "end": v(-20.56, -2.86) * mm});
            skLineSegment(sketch, "E16.20.9", {"start": v(-20.33, -2.18) * mm, "end": v(-19.89, -2.12) * mm});
            skArc(sketch, "E16.20.10", {"start": v(-20.61, -2.79) * mm, "mid": v(-20.6, -2.83) * mm, "end": v(-20.56, -2.86) * mm});
            skArc(sketch, "E16.20.11", {"start": v(-20.35, -2.99) * mm, "mid": v(-20.3, -3.01) * mm, "end": v(-20.23, -3.01) * mm});
            skArc(sketch, "E16.20.12", {"start": v(-20.65, -2.5) * mm, "mid": v(-20.65, -2.45) * mm, "end": v(-20.62, -2.41) * mm});
            skArc(sketch, "E16.20.13", {"start": v(-20.45, -2.24) * mm, "mid": v(-20.4, -2.2) * mm, "end": v(-20.33, -2.18) * mm});
            skLineSegment(sketch, "E16.20.14", {"start": v(-20.63, -2.64) * mm, "end": v(-20.61, -2.79) * mm});
            skPoint(sketch, "E16.21.0", {"position": v(-19.96, -4.73) * mm});
            skLineSegment(sketch, "E16.21.1", {"start": v(-20.18, -3.96) * mm, "end": v(-20.34, -4.15) * mm});
            skPoint(sketch, "E16.21.2", {"position": v(-20.14, -3.91) * mm});
            skLineSegment(sketch, "E16.21.3", {"start": v(-20.33, -4.38) * mm, "end": v(-19.55, -4.21) * mm});
            skLineSegment(sketch, "E16.21.4", {"start": v(-19.9, -4.72) * mm, "end": v(-19.46, -4.62) * mm});
            skPoint(sketch, "E16.21.5", {"position": v(-20.38, -4.19) * mm});
            skLineSegment(sketch, "E16.21.6", {"start": v(-20.33, -4.38) * mm, "end": v(-20.37, -4.24) * mm});
            skPoint(sketch, "E16.21.7", {"position": v(-20.3, -4.58) * mm});
            skLineSegment(sketch, "E16.21.8", {"start": v(-20.03, -4.7) * mm, "end": v(-20.25, -4.6) * mm});
            skLineSegment(sketch, "E16.21.9", {"start": v(-20.07, -3.9) * mm, "end": v(-19.64, -3.8) * mm});
            skArc(sketch, "E16.21.10", {"start": v(-20.3, -4.53) * mm, "mid": v(-20.28, -4.57) * mm, "end": v(-20.25, -4.6) * mm});
            skArc(sketch, "E16.21.11", {"start": v(-20.03, -4.7) * mm, "mid": v(-19.96, -4.72) * mm, "end": v(-19.9, -4.72) * mm});
            skArc(sketch, "E16.21.12", {"start": v(-20.37, -4.24) * mm, "mid": v(-20.36, -4.2) * mm, "end": v(-20.34, -4.15) * mm});
            skArc(sketch, "E16.21.13", {"start": v(-20.18, -3.96) * mm, "mid": v(-20.13, -3.92) * mm, "end": v(-20.07, -3.9) * mm});
            skLineSegment(sketch, "E16.21.14", {"start": v(-20.33, -4.38) * mm, "end": v(-20.3, -4.53) * mm});
            skPoint(sketch, "E16.22.0", {"position": v(-19.5, -6.4) * mm});
            skLineSegment(sketch, "E16.22.1", {"start": v(-19.78, -5.66) * mm, "end": v(-19.92, -5.86) * mm});
            skPoint(sketch, "E16.22.2", {"position": v(-19.74, -5.6) * mm});
            skLineSegment(sketch, "E16.22.3", {"start": v(-19.89, -6.1) * mm, "end": v(-19.12, -5.86) * mm});
            skLineSegment(sketch, "E16.22.4", {"start": v(-19.43, -6.39) * mm, "end": v(-19, -6.26) * mm});
            skPoint(sketch, "E16.22.5", {"position": v(-19.95, -5.9) * mm});
            skLineSegment(sketch, "E16.22.6", {"start": v(-19.89, -6.1) * mm, "end": v(-19.93, -5.95) * mm});
            skPoint(sketch, "E16.22.7", {"position": v(-19.83, -6.28) * mm});
            skLineSegment(sketch, "E16.22.8", {"start": v(-19.55, -6.38) * mm, "end": v(-19.78, -6.3) * mm});
            skLineSegment(sketch, "E16.22.9", {"start": v(-19.67, -5.59) * mm, "end": v(-19.24, -5.45) * mm});
            skArc(sketch, "E16.22.10", {"start": v(-19.85, -6.23) * mm, "mid": v(-19.82, -6.27) * mm, "end": v(-19.78, -6.3) * mm});
            skArc(sketch, "E16.22.11", {"start": v(-19.55, -6.38) * mm, "mid": v(-19.5, -6.4) * mm, "end": v(-19.43, -6.39) * mm});
            skArc(sketch, "E16.22.12", {"start": v(-19.93, -5.95) * mm, "mid": v(-19.94, -5.9) * mm, "end": v(-19.92, -5.86) * mm});
            skArc(sketch, "E16.22.13", {"start": v(-19.78, -5.66) * mm, "mid": v(-19.73, -5.61) * mm, "end": v(-19.67, -5.59) * mm});
            skLineSegment(sketch, "E16.22.14", {"start": v(-19.89, -6.1) * mm, "end": v(-19.85, -6.23) * mm});
            skPoint(sketch, "E16.23.0", {"position": v(-18.88, -8.04) * mm});
            skLineSegment(sketch, "E16.23.1", {"start": v(-19.22, -7.32) * mm, "end": v(-19.35, -7.53) * mm});
            skPoint(sketch, "E16.23.2", {"position": v(-19.19, -7.26) * mm});
            skLineSegment(sketch, "E16.23.3", {"start": v(-19.3, -7.76) * mm, "end": v(-18.56, -7.46) * mm});
            skLineSegment(sketch, "E16.23.4", {"start": v(-18.81, -8.01) * mm, "end": v(-18.4, -7.84) * mm});
            skPoint(sketch, "E16.23.5", {"position": v(-19.37, -7.57) * mm});
            skLineSegment(sketch, "E16.23.6", {"start": v(-19.3, -7.76) * mm, "end": v(-19.36, -7.62) * mm});
            skPoint(sketch, "E16.23.7", {"position": v(-19.23, -7.94) * mm});
            skLineSegment(sketch, "E16.23.8", {"start": v(-18.94, -8.02) * mm, "end": v(-19.18, -7.95) * mm});
            skLineSegment(sketch, "E16.23.9", {"start": v(-19.13, -7.23) * mm, "end": v(-18.71, -7.07) * mm});
            skArc(sketch, "E16.23.10", {"start": v(-19.25, -7.9) * mm, "mid": v(-19.22, -7.93) * mm, "end": v(-19.18, -7.95) * mm});
            skArc(sketch, "E16.23.11", {"start": v(-18.94, -8.02) * mm, "mid": v(-18.88, -8.03) * mm, "end": v(-18.81, -8.01) * mm});
            skArc(sketch, "E16.23.12", {"start": v(-19.36, -7.62) * mm, "mid": v(-19.36, -7.57) * mm, "end": v(-19.35, -7.53) * mm});
            skArc(sketch, "E16.23.13", {"start": v(-19.22, -7.32) * mm, "mid": v(-19.18, -7.27) * mm, "end": v(-19.13, -7.23) * mm});
            skLineSegment(sketch, "E16.23.14", {"start": v(-19.3, -7.76) * mm, "end": v(-19.25, -7.9) * mm});
            skPoint(sketch, "E16.24.0", {"position": v(-18.13, -9.6) * mm});
            skLineSegment(sketch, "E16.24.1", {"start": v(-18.53, -8.92) * mm, "end": v(-18.64, -9.14) * mm});
            skPoint(sketch, "E16.24.2", {"position": v(-18.5, -8.86) * mm});
            skLineSegment(sketch, "E16.24.3", {"start": v(-18.57, -9.36) * mm, "end": v(-17.86, -9) * mm});
            skLineSegment(sketch, "E16.24.4", {"start": v(-18.07, -9.58) * mm, "end": v(-17.67, -9.38) * mm});
            skPoint(sketch, "E16.24.5", {"position": v(-18.66, -9.19) * mm});
            skLineSegment(sketch, "E16.24.6", {"start": v(-18.57, -9.36) * mm, "end": v(-18.64, -9.23) * mm});
            skPoint(sketch, "E16.24.7", {"position": v(-18.48, -9.54) * mm});
            skLineSegment(sketch, "E16.24.8", {"start": v(-18.2, -9.6) * mm, "end": v(-18.44, -9.55) * mm});
            skLineSegment(sketch, "E16.24.9", {"start": v(-18.44, -8.83) * mm, "end": v(-18.04, -8.63) * mm});
            skArc(sketch, "E16.24.10", {"start": v(-18.5, -9.5) * mm, "mid": v(-18.48, -9.53) * mm, "end": v(-18.44, -9.55) * mm});
            skArc(sketch, "E16.24.11", {"start": v(-18.2, -9.6) * mm, "mid": v(-18.13, -9.6) * mm, "end": v(-18.07, -9.58) * mm});
            skArc(sketch, "E16.24.12", {"start": v(-18.64, -9.23) * mm, "mid": v(-18.65, -9.19) * mm, "end": v(-18.64, -9.14) * mm});
            skArc(sketch, "E16.24.13", {"start": v(-18.53, -8.92) * mm, "mid": v(-18.5, -8.87) * mm, "end": v(-18.44, -8.83) * mm});
            skLineSegment(sketch, "E16.24.14", {"start": v(-18.57, -9.36) * mm, "end": v(-18.5, -9.5) * mm});
            skPoint(sketch, "E16.25.0", {"position": v(-17.25, -11.11) * mm});
            skLineSegment(sketch, "E16.25.1", {"start": v(-17.71, -10.46) * mm, "end": v(-17.8, -10.7) * mm});
            skPoint(sketch, "E16.25.2", {"position": v(-17.69, -10.4) * mm});
            skLineSegment(sketch, "E16.25.3", {"start": v(-17.71, -10.9) * mm, "end": v(-17.03, -10.49) * mm});
            skLineSegment(sketch, "E16.25.4", {"start": v(-17.19, -11.08) * mm, "end": v(-16.8, -10.84) * mm});
            skPoint(sketch, "E16.25.5", {"position": v(-17.82, -10.74) * mm});
            skLineSegment(sketch, "E16.25.6", {"start": v(-17.71, -10.9) * mm, "end": v(-17.8, -10.78) * mm});
            skPoint(sketch, "E16.25.7", {"position": v(-17.6, -11.07) * mm});
            skLineSegment(sketch, "E16.25.8", {"start": v(-17.31, -11.1) * mm, "end": v(-17.56, -11.08) * mm});
            skLineSegment(sketch, "E16.25.9", {"start": v(-17.63, -10.36) * mm, "end": v(-17.25, -10.13) * mm});
            skArc(sketch, "E16.25.10", {"start": v(-17.63, -11.03) * mm, "mid": v(-17.6, -11.07) * mm, "end": v(-17.56, -11.08) * mm});
            skArc(sketch, "E16.25.11", {"start": v(-17.31, -11.1) * mm, "mid": v(-17.25, -11.1) * mm, "end": v(-17.19, -11.08) * mm});
            skArc(sketch, "E16.25.12", {"start": v(-17.8, -10.78) * mm, "mid": v(-17.8, -10.74) * mm, "end": v(-17.8, -10.7) * mm});
            skArc(sketch, "E16.25.13", {"start": v(-17.71, -10.46) * mm, "mid": v(-17.68, -10.4) * mm, "end": v(-17.63, -10.36) * mm});
            skLineSegment(sketch, "E16.25.14", {"start": v(-17.71, -10.9) * mm, "end": v(-17.63, -11.03) * mm});
            skPoint(sketch, "E16.26.0", {"position": v(-16.24, -12.53) * mm});
            skLineSegment(sketch, "E16.26.1", {"start": v(-16.76, -11.93) * mm, "end": v(-16.83, -12.16) * mm});
            skPoint(sketch, "E16.26.2", {"position": v(-16.74, -11.86) * mm});
            skLineSegment(sketch, "E16.26.3", {"start": v(-16.72, -12.37) * mm, "end": v(-16.08, -11.9) * mm});
            skLineSegment(sketch, "E16.26.4", {"start": v(-16.19, -12.5) * mm, "end": v(-15.83, -12.23) * mm});
            skPoint(sketch, "E16.26.5", {"position": v(-16.84, -12.2) * mm});
            skLineSegment(sketch, "E16.26.6", {"start": v(-16.72, -12.37) * mm, "end": v(-16.81, -12.25) * mm});
            skPoint(sketch, "E16.26.7", {"position": v(-16.6, -12.53) * mm});
            skLineSegment(sketch, "E16.26.8", {"start": v(-16.31, -12.53) * mm, "end": v(-16.56, -12.53) * mm});
            skLineSegment(sketch, "E16.26.9", {"start": v(-16.69, -11.82) * mm, "end": v(-16.33, -11.55) * mm});
            skArc(sketch, "E16.26.10", {"start": v(-16.63, -12.49) * mm, "mid": v(-16.6, -12.52) * mm, "end": v(-16.56, -12.53) * mm});
            skArc(sketch, "E16.26.11", {"start": v(-16.31, -12.53) * mm, "mid": v(-16.25, -12.52) * mm, "end": v(-16.19, -12.5) * mm});
            skArc(sketch, "E16.26.12", {"start": v(-16.81, -12.25) * mm, "mid": v(-16.83, -12.2) * mm, "end": v(-16.83, -12.16) * mm});
            skArc(sketch, "E16.26.13", {"start": v(-16.76, -11.93) * mm, "mid": v(-16.73, -11.87) * mm, "end": v(-16.69, -11.82) * mm});
            skLineSegment(sketch, "E16.26.14", {"start": v(-16.72, -12.37) * mm, "end": v(-16.63, -12.49) * mm});
            skPoint(sketch, "E16.27.0", {"position": v(-15.12, -13.87) * mm});
            skLineSegment(sketch, "E16.27.1", {"start": v(-15.69, -13.3) * mm, "end": v(-15.74, -13.55) * mm});
            skPoint(sketch, "E16.27.2", {"position": v(-15.68, -13.24) * mm});
            skLineSegment(sketch, "E16.27.3", {"start": v(-15.61, -13.74) * mm, "end": v(-15.01, -13.21) * mm});
            skLineSegment(sketch, "E16.27.4", {"start": v(-15.07, -13.82) * mm, "end": v(-14.73, -13.53) * mm});
            skPoint(sketch, "E16.27.5", {"position": v(-15.75, -13.6) * mm});
            skLineSegment(sketch, "E16.27.6", {"start": v(-15.61, -13.74) * mm, "end": v(-15.71, -13.63) * mm});
            skPoint(sketch, "E16.27.7", {"position": v(-15.48, -13.9) * mm});
            skLineSegment(sketch, "E16.27.8", {"start": v(-15.19, -13.87) * mm, "end": v(-15.43, -13.89) * mm});
            skLineSegment(sketch, "E16.27.9", {"start": v(-15.62, -13.2) * mm, "end": v(-15.29, -12.9) * mm});
            skArc(sketch, "E16.27.10", {"start": v(-15.52, -13.85) * mm, "mid": v(-15.48, -13.88) * mm, "end": v(-15.43, -13.89) * mm});
            skArc(sketch, "E16.27.11", {"start": v(-15.19, -13.87) * mm, "mid": v(-15.13, -13.86) * mm, "end": v(-15.07, -13.82) * mm});
            skArc(sketch, "E16.27.12", {"start": v(-15.71, -13.63) * mm, "mid": v(-15.73, -13.6) * mm, "end": v(-15.74, -13.55) * mm});
            skArc(sketch, "E16.27.13", {"start": v(-15.69, -13.3) * mm, "mid": v(-15.67, -13.24) * mm, "end": v(-15.62, -13.2) * mm});
            skLineSegment(sketch, "E16.27.14", {"start": v(-15.61, -13.74) * mm, "end": v(-15.52, -13.85) * mm});
            skPoint(sketch, "E16.28.0", {"position": v(-13.9, -15.1) * mm});
            skLineSegment(sketch, "E16.28.1", {"start": v(-14.5, -14.59) * mm, "end": v(-14.53, -14.83) * mm});
            skPoint(sketch, "E16.28.2", {"position": v(-14.5, -14.52) * mm});
            skLineSegment(sketch, "E16.28.3", {"start": v(-14.4, -15.02) * mm, "end": v(-13.84, -14.44) * mm});
            skLineSegment(sketch, "E16.28.4", {"start": v(-13.84, -15.05) * mm, "end": v(-13.53, -14.73) * mm});
            skPoint(sketch, "E16.28.5", {"position": v(-14.54, -14.88) * mm});
            skLineSegment(sketch, "E16.28.6", {"start": v(-14.4, -15.02) * mm, "end": v(-14.5, -14.91) * mm});
            skPoint(sketch, "E16.28.7", {"position": v(-14.25, -15.15) * mm});
            skLineSegment(sketch, "E16.28.8", {"start": v(-13.96, -15.1) * mm, "end": v(-14.2, -15.15) * mm});
            skLineSegment(sketch, "E16.28.9", {"start": v(-14.45, -14.47) * mm, "end": v(-14.14, -14.15) * mm});
            skArc(sketch, "E16.28.10", {"start": v(-14.29, -15.12) * mm, "mid": v(-14.25, -15.14) * mm, "end": v(-14.2, -15.15) * mm});
            skArc(sketch, "E16.28.11", {"start": v(-13.96, -15.1) * mm, "mid": v(-13.9, -15.09) * mm, "end": v(-13.84, -15.05) * mm});
            skArc(sketch, "E16.28.12", {"start": v(-14.5, -14.91) * mm, "mid": v(-14.53, -14.88) * mm, "end": v(-14.53, -14.83) * mm});
            skArc(sketch, "E16.28.13", {"start": v(-14.5, -14.59) * mm, "mid": v(-14.49, -14.52) * mm, "end": v(-14.45, -14.47) * mm});
            skLineSegment(sketch, "E16.28.14", {"start": v(-14.4, -15.02) * mm, "end": v(-14.29, -15.12) * mm});
            skPoint(sketch, "E16.29.0", {"position": v(-12.56, -16.22) * mm});
            skLineSegment(sketch, "E16.29.1", {"start": v(-13.21, -15.76) * mm, "end": v(-13.22, -16) * mm});
            skPoint(sketch, "E16.29.2", {"position": v(-13.21, -15.7) * mm});
            skLineSegment(sketch, "E16.29.3", {"start": v(-13.07, -16.18) * mm, "end": v(-12.56, -15.56) * mm});
            skLineSegment(sketch, "E16.29.4", {"start": v(-12.52, -16.17) * mm, "end": v(-12.24, -15.82) * mm});
            skPoint(sketch, "E16.29.5", {"position": v(-13.22, -16.06) * mm});
            skLineSegment(sketch, "E16.29.6", {"start": v(-13.07, -16.18) * mm, "end": v(-13.18, -16.09) * mm});
            skPoint(sketch, "E16.29.7", {"position": v(-12.91, -16.3) * mm});
            skLineSegment(sketch, "E16.29.8", {"start": v(-12.63, -16.24) * mm, "end": v(-12.87, -16.3) * mm});
            skLineSegment(sketch, "E16.29.9", {"start": v(-13.17, -15.64) * mm, "end": v(-12.89, -15.3) * mm});
            skArc(sketch, "E16.29.10", {"start": v(-12.95, -16.28) * mm, "mid": v(-12.91, -16.3) * mm, "end": v(-12.87, -16.3) * mm});
            skArc(sketch, "E16.29.11", {"start": v(-12.63, -16.24) * mm, "mid": v(-12.57, -16.21) * mm, "end": v(-12.52, -16.17) * mm});
            skArc(sketch, "E16.29.12", {"start": v(-13.18, -16.09) * mm, "mid": v(-13.21, -16.05) * mm, "end": v(-13.22, -16) * mm});
            skArc(sketch, "E16.29.13", {"start": v(-13.21, -15.76) * mm, "mid": v(-13.2, -15.7) * mm, "end": v(-13.17, -15.64) * mm});
            skLineSegment(sketch, "E16.29.14", {"start": v(-13.07, -16.18) * mm, "end": v(-12.95, -16.28) * mm});
            skPoint(sketch, "E16.30.0", {"position": v(-11.14, -17.23) * mm});
            skLineSegment(sketch, "E16.30.1", {"start": v(-11.83, -16.83) * mm, "end": v(-11.82, -17.07) * mm});
            skPoint(sketch, "E16.30.2", {"position": v(-11.83, -16.76) * mm});
            skLineSegment(sketch, "E16.30.3", {"start": v(-11.65, -17.23) * mm, "end": v(-11.2, -16.57) * mm});
            skLineSegment(sketch, "E16.30.4", {"start": v(-11.1, -17.17) * mm, "end": v(-10.85, -16.8) * mm});
            skPoint(sketch, "E16.30.5", {"position": v(-11.81, -17.12) * mm});
            skLineSegment(sketch, "E16.30.6", {"start": v(-11.65, -17.23) * mm, "end": v(-11.77, -17.15) * mm});
            skPoint(sketch, "E16.30.7", {"position": v(-11.48, -17.34) * mm});
            skLineSegment(sketch, "E16.30.8", {"start": v(-11.2, -17.25) * mm, "end": v(-11.44, -17.33) * mm});
            skLineSegment(sketch, "E16.30.9", {"start": v(-11.8, -16.7) * mm, "end": v(-11.54, -16.33) * mm});
            skArc(sketch, "E16.30.10", {"start": v(-11.52, -17.32) * mm, "mid": v(-11.48, -17.33) * mm, "end": v(-11.44, -17.33) * mm});
            skArc(sketch, "E16.30.11", {"start": v(-11.2, -17.25) * mm, "mid": v(-11.15, -17.22) * mm, "end": v(-11.1, -17.17) * mm});
            skArc(sketch, "E16.30.12", {"start": v(-11.77, -17.15) * mm, "mid": v(-11.8, -17.12) * mm, "end": v(-11.82, -17.07) * mm});
            skArc(sketch, "E16.30.13", {"start": v(-11.83, -16.83) * mm, "mid": v(-11.82, -16.76) * mm, "end": v(-11.8, -16.7) * mm});
            skLineSegment(sketch, "E16.30.14", {"start": v(-11.65, -17.23) * mm, "end": v(-11.52, -17.32) * mm});
            skPoint(sketch, "E16.31.0", {"position": v(-9.64, -18.11) * mm});
            skLineSegment(sketch, "E16.31.1", {"start": v(-10.36, -17.77) * mm, "end": v(-10.32, -18.01) * mm});
            skPoint(sketch, "E16.31.2", {"position": v(-10.37, -17.7) * mm});
            skLineSegment(sketch, "E16.31.3", {"start": v(-10.14, -18.16) * mm, "end": v(-9.75, -17.46) * mm});
            skLineSegment(sketch, "E16.31.4", {"start": v(-9.6, -18.05) * mm, "end": v(-9.39, -17.66) * mm});
            skPoint(sketch, "E16.31.5", {"position": v(-10.32, -18.06) * mm});
            skLineSegment(sketch, "E16.31.6", {"start": v(-10.14, -18.16) * mm, "end": v(-10.27, -18.09) * mm});
            skPoint(sketch, "E16.31.7", {"position": v(-9.97, -18.26) * mm});
            skLineSegment(sketch, "E16.31.8", {"start": v(-9.7, -18.14) * mm, "end": v(-9.93, -18.24) * mm});
            skLineSegment(sketch, "E16.31.9", {"start": v(-10.34, -17.64) * mm, "end": v(-10.12, -17.25) * mm});
            skArc(sketch, "E16.31.10", {"start": v(-10.01, -18.23) * mm, "mid": v(-9.97, -18.24) * mm, "end": v(-9.93, -18.24) * mm});
            skArc(sketch, "E16.31.11", {"start": v(-9.7, -18.14) * mm, "mid": v(-9.65, -18.1) * mm, "end": v(-9.6, -18.05) * mm});
            skArc(sketch, "E16.31.12", {"start": v(-10.27, -18.09) * mm, "mid": v(-10.3, -18.06) * mm, "end": v(-10.32, -18.01) * mm});
            skArc(sketch, "E16.31.13", {"start": v(-10.36, -17.77) * mm, "mid": v(-10.36, -17.7) * mm, "end": v(-10.34, -17.64) * mm});
            skLineSegment(sketch, "E16.31.14", {"start": v(-10.14, -18.16) * mm, "end": v(-10.01, -18.23) * mm});
            skPoint(sketch, "E16.32.0", {"position": v(-8.07, -18.86) * mm});
            skPoint(sketch, "E16.32.2", {"position": v(-8.83, -18.52) * mm});
            skLineSegment(sketch, "E16.32.3", {"start": v(-8.57, -18.95) * mm, "end": v(-8.24, -18.23) * mm});
            skLineSegment(sketch, "E16.32.4", {"start": v(-8.04, -18.8) * mm, "end": v(-7.85, -18.4) * mm});
            skPoint(sketch, "E16.32.5", {"position": v(-8.75, -18.87) * mm});
            skPoint(sketch, "E16.32.7", {"position": v(-8.39, -19.04) * mm});
            skLineSegment(sketch, "E16.32.9", {"start": v(-8.8, -18.46) * mm, "end": v(-8.62, -18.05) * mm});
            skArc(sketch, "E16.32.12", {"start": v(-8.7, -18.9) * mm, "mid": v(-8.74, -18.87) * mm, "end": v(-8.76, -18.82) * mm});
            skPoint(sketch, "E16.33.0", {"position": v(-6.44, -19.48) * mm});
            skPoint(sketch, "E16.33.2", {"position": v(-7.23, -19.2) * mm});
            skLineSegment(sketch, "E16.33.9", {"start": v(-7.2, -19.14) * mm, "end": v(-7.06, -18.71) * mm});
            skPoint(sketch, "E16.34.2", {"position": v(-5.57, -19.75) * mm});
            skPoint(sketch, "E16.34.5", {"position": v(-5.43, -20.08) * mm});
            skLineSegment(sketch, "E16.34.9", {"start": v(-5.56, -19.68) * mm, "end": v(-5.44, -19.24) * mm});
            skLineSegment(sketch, "E16.35.9", {"start": v(-3.87, -20.08) * mm, "end": v(-3.8, -19.64) * mm});
            skLineSegment(sketch, "E16.36.9", {"start": v(-2.15, -20.34) * mm, "end": v(-2.11, -19.89) * mm});
            skLineSegment(sketch, "E16.37.9", {"start": v(-0.42, -20.44) * mm, "end": v(-0.42, -20) * mm});
            skPoint(sketch, "E16.38.5", {"position": v(1.57, -20.74) * mm});
            skLineSegment(sketch, "E16.38.6", {"start": v(1.76, -20.73) * mm, "end": v(1.62, -20.74) * mm});
            skLineSegment(sketch, "E16.38.9", {"start": v(1.32, -20.4) * mm, "end": v(1.28, -19.96) * mm});
            skArc(sketch, "E16.38.12", {"start": v(1.62, -20.74) * mm, "mid": v(1.57, -20.73) * mm, "end": v(1.53, -20.7) * mm});
            skArc(sketch, "E16.38.13", {"start": v(1.37, -20.52) * mm, "mid": v(1.33, -20.47) * mm, "end": v(1.32, -20.4) * mm});
            skLineSegment(sketch, "E16.39.3", {"start": v(3.52, -20.5) * mm, "end": v(3.38, -19.71) * mm});
            skPoint(sketch, "E16.39.5", {"position": v(3.32, -20.53) * mm});
            skLineSegment(sketch, "E16.39.9", {"start": v(3.04, -20.22) * mm, "end": v(2.97, -19.78) * mm});
            skLineSegment(sketch, "E16.39.14", {"start": v(3.52, -20.5) * mm, "end": v(3.66, -20.48) * mm});
            skLineSegment(sketch, "E16.40.1", {"start": v(4.82, -20) * mm, "end": v(5.01, -20.15) * mm});
            skArc(sketch, "E16.40.12", {"start": v(5.1, -20.17) * mm, "mid": v(5.05, -20.17) * mm, "end": v(5.01, -20.15) * mm});
            skArc(sketch, "E16.40.13", {"start": v(4.82, -20) * mm, "mid": v(4.77, -19.95) * mm, "end": v(4.75, -19.9) * mm});
            skPoint(sketch, "E16.41.0", {"position": v(7.23, -19.2) * mm});
            skPoint(sketch, "E16.41.2", {"position": v(6.44, -19.48) * mm});
            skLineSegment(sketch, "E16.41.9", {"start": v(6.42, -19.42) * mm, "end": v(6.27, -19) * mm});
            skArc(sketch, "E16.41.13", {"start": v(6.5, -19.52) * mm, "mid": v(6.45, -19.47) * mm, "end": v(6.42, -19.42) * mm});
            skPoint(sketch, "E16.42.0", {"position": v(8.83, -18.52) * mm});
            skPoint(sketch, "E16.42.2", {"position": v(8.07, -18.86) * mm});
            skLineSegment(sketch, "E16.42.3", {"start": v(8.57, -18.95) * mm, "end": v(8.24, -18.23) * mm});
            skLineSegment(sketch, "E16.42.4", {"start": v(8.8, -18.46) * mm, "end": v(8.62, -18.05) * mm});
            skPoint(sketch, "E16.42.5", {"position": v(8.39, -19.04) * mm});
            skPoint(sketch, "E16.42.7", {"position": v(8.75, -18.87) * mm});
            skLineSegment(sketch, "E16.42.9", {"start": v(8.04, -18.8) * mm, "end": v(7.85, -18.4) * mm});
            skArc(sketch, "E16.42.13", {"start": v(8.13, -18.9) * mm, "mid": v(8.08, -18.86) * mm, "end": v(8.04, -18.8) * mm});
            skPoint(sketch, "E16.43.0", {"position": v(10.37, -17.7) * mm});
            skLineSegment(sketch, "E16.43.1", {"start": v(9.7, -18.14) * mm, "end": v(9.93, -18.24) * mm});
            skPoint(sketch, "E16.43.2", {"position": v(9.64, -18.11) * mm});
            skLineSegment(sketch, "E16.43.3", {"start": v(10.14, -18.16) * mm, "end": v(9.75, -17.46) * mm});
            skLineSegment(sketch, "E16.43.4", {"start": v(10.34, -17.64) * mm, "end": v(10.12, -17.25) * mm});
            skPoint(sketch, "E16.43.5", {"position": v(9.97, -18.26) * mm});
            skLineSegment(sketch, "E16.43.6", {"start": v(10.14, -18.16) * mm, "end": v(10.01, -18.23) * mm});
            skPoint(sketch, "E16.43.7", {"position": v(10.32, -18.06) * mm});
            skLineSegment(sketch, "E16.43.8", {"start": v(10.36, -17.77) * mm, "end": v(10.32, -18.01) * mm});
            skLineSegment(sketch, "E16.43.9", {"start": v(9.6, -18.05) * mm, "end": v(9.39, -17.66) * mm});
            skArc(sketch, "E16.43.10", {"start": v(10.27, -18.09) * mm, "mid": v(10.3, -18.06) * mm, "end": v(10.32, -18.01) * mm});
            skArc(sketch, "E16.43.11", {"start": v(10.36, -17.77) * mm, "mid": v(10.36, -17.7) * mm, "end": v(10.34, -17.64) * mm});
            skArc(sketch, "E16.43.12", {"start": v(10.01, -18.23) * mm, "mid": v(9.97, -18.24) * mm, "end": v(9.93, -18.24) * mm});
            skArc(sketch, "E16.43.13", {"start": v(9.7, -18.14) * mm, "mid": v(9.65, -18.1) * mm, "end": v(9.6, -18.05) * mm});
            skLineSegment(sketch, "E16.43.14", {"start": v(10.14, -18.16) * mm, "end": v(10.27, -18.09) * mm});
            skPoint(sketch, "E16.44.0", {"position": v(11.83, -16.76) * mm});
            skLineSegment(sketch, "E16.44.1", {"start": v(11.2, -17.25) * mm, "end": v(11.44, -17.33) * mm});
            skPoint(sketch, "E16.44.2", {"position": v(11.14, -17.23) * mm});
            skLineSegment(sketch, "E16.44.3", {"start": v(11.65, -17.23) * mm, "end": v(11.2, -16.57) * mm});
            skLineSegment(sketch, "E16.44.4", {"start": v(11.8, -16.7) * mm, "end": v(11.54, -16.33) * mm});
            skPoint(sketch, "E16.44.5", {"position": v(11.48, -17.34) * mm});
            skLineSegment(sketch, "E16.44.6", {"start": v(11.65, -17.23) * mm, "end": v(11.52, -17.32) * mm});
            skPoint(sketch, "E16.44.7", {"position": v(11.81, -17.12) * mm});
            skLineSegment(sketch, "E16.44.8", {"start": v(11.83, -16.83) * mm, "end": v(11.82, -17.07) * mm});
            skLineSegment(sketch, "E16.44.9", {"start": v(11.1, -17.17) * mm, "end": v(10.85, -16.8) * mm});
            skArc(sketch, "E16.44.10", {"start": v(11.77, -17.15) * mm, "mid": v(11.8, -17.12) * mm, "end": v(11.82, -17.07) * mm});
            skArc(sketch, "E16.44.11", {"start": v(11.83, -16.83) * mm, "mid": v(11.82, -16.76) * mm, "end": v(11.8, -16.7) * mm});
            skArc(sketch, "E16.44.12", {"start": v(11.52, -17.32) * mm, "mid": v(11.48, -17.33) * mm, "end": v(11.44, -17.33) * mm});
            skArc(sketch, "E16.44.13", {"start": v(11.2, -17.25) * mm, "mid": v(11.15, -17.22) * mm, "end": v(11.1, -17.17) * mm});
            skLineSegment(sketch, "E16.44.14", {"start": v(11.65, -17.23) * mm, "end": v(11.77, -17.15) * mm});
            skPoint(sketch, "E16.45.0", {"position": v(13.21, -15.7) * mm});
            skLineSegment(sketch, "E16.45.1", {"start": v(12.63, -16.24) * mm, "end": v(12.87, -16.3) * mm});
            skPoint(sketch, "E16.45.2", {"position": v(12.56, -16.22) * mm});
            skLineSegment(sketch, "E16.45.3", {"start": v(13.07, -16.18) * mm, "end": v(12.56, -15.56) * mm});
            skLineSegment(sketch, "E16.45.4", {"start": v(13.17, -15.64) * mm, "end": v(12.89, -15.3) * mm});
            skPoint(sketch, "E16.45.5", {"position": v(12.91, -16.3) * mm});
            skLineSegment(sketch, "E16.45.6", {"start": v(13.07, -16.18) * mm, "end": v(12.95, -16.28) * mm});
            skPoint(sketch, "E16.45.7", {"position": v(13.22, -16.06) * mm});
            skLineSegment(sketch, "E16.45.8", {"start": v(13.21, -15.76) * mm, "end": v(13.22, -16) * mm});
            skLineSegment(sketch, "E16.45.9", {"start": v(12.52, -16.17) * mm, "end": v(12.24, -15.82) * mm});
            skArc(sketch, "E16.45.10", {"start": v(13.18, -16.09) * mm, "mid": v(13.21, -16.05) * mm, "end": v(13.22, -16) * mm});
            skArc(sketch, "E16.45.11", {"start": v(13.21, -15.76) * mm, "mid": v(13.2, -15.7) * mm, "end": v(13.17, -15.64) * mm});
            skArc(sketch, "E16.45.12", {"start": v(12.95, -16.28) * mm, "mid": v(12.91, -16.3) * mm, "end": v(12.87, -16.3) * mm});
            skArc(sketch, "E16.45.13", {"start": v(12.63, -16.24) * mm, "mid": v(12.57, -16.21) * mm, "end": v(12.52, -16.17) * mm});
            skLineSegment(sketch, "E16.45.14", {"start": v(13.07, -16.18) * mm, "end": v(13.18, -16.09) * mm});
            skPoint(sketch, "E16.46.0", {"position": v(14.5, -14.52) * mm});
            skLineSegment(sketch, "E16.46.1", {"start": v(13.96, -15.1) * mm, "end": v(14.2, -15.15) * mm});
            skPoint(sketch, "E16.46.2", {"position": v(13.9, -15.1) * mm});
            skLineSegment(sketch, "E16.46.3", {"start": v(14.4, -15.02) * mm, "end": v(13.84, -14.44) * mm});
            skLineSegment(sketch, "E16.46.4", {"start": v(14.45, -14.47) * mm, "end": v(14.14, -14.15) * mm});
            skPoint(sketch, "E16.46.5", {"position": v(14.25, -15.15) * mm});
            skLineSegment(sketch, "E16.46.6", {"start": v(14.4, -15.02) * mm, "end": v(14.29, -15.12) * mm});
            skPoint(sketch, "E16.46.7", {"position": v(14.54, -14.88) * mm});
            skLineSegment(sketch, "E16.46.8", {"start": v(14.5, -14.59) * mm, "end": v(14.53, -14.83) * mm});
            skLineSegment(sketch, "E16.46.9", {"start": v(13.84, -15.05) * mm, "end": v(13.53, -14.73) * mm});
            skArc(sketch, "E16.46.10", {"start": v(14.5, -14.91) * mm, "mid": v(14.53, -14.88) * mm, "end": v(14.53, -14.83) * mm});
            skArc(sketch, "E16.46.11", {"start": v(14.5, -14.59) * mm, "mid": v(14.49, -14.52) * mm, "end": v(14.45, -14.47) * mm});
            skArc(sketch, "E16.46.12", {"start": v(14.29, -15.12) * mm, "mid": v(14.25, -15.14) * mm, "end": v(14.2, -15.15) * mm});
            skArc(sketch, "E16.46.13", {"start": v(13.96, -15.1) * mm, "mid": v(13.9, -15.09) * mm, "end": v(13.84, -15.05) * mm});
            skLineSegment(sketch, "E16.46.14", {"start": v(14.4, -15.02) * mm, "end": v(14.5, -14.91) * mm});
            skPoint(sketch, "E16.47.0", {"position": v(15.68, -13.24) * mm});
            skLineSegment(sketch, "E16.47.1", {"start": v(15.19, -13.87) * mm, "end": v(15.43, -13.89) * mm});
            skPoint(sketch, "E16.47.2", {"position": v(15.12, -13.87) * mm});
            skLineSegment(sketch, "E16.47.3", {"start": v(15.61, -13.74) * mm, "end": v(15.01, -13.21) * mm});
            skLineSegment(sketch, "E16.47.4", {"start": v(15.62, -13.2) * mm, "end": v(15.29, -12.9) * mm});
            skPoint(sketch, "E16.47.5", {"position": v(15.48, -13.9) * mm});
            skLineSegment(sketch, "E16.47.6", {"start": v(15.61, -13.74) * mm, "end": v(15.52, -13.85) * mm});
            skPoint(sketch, "E16.47.7", {"position": v(15.75, -13.6) * mm});
            skLineSegment(sketch, "E16.47.8", {"start": v(15.69, -13.3) * mm, "end": v(15.74, -13.55) * mm});
            skLineSegment(sketch, "E16.47.9", {"start": v(15.07, -13.82) * mm, "end": v(14.73, -13.53) * mm});
            skArc(sketch, "E16.47.10", {"start": v(15.71, -13.63) * mm, "mid": v(15.73, -13.6) * mm, "end": v(15.74, -13.55) * mm});
            skArc(sketch, "E16.47.11", {"start": v(15.69, -13.3) * mm, "mid": v(15.67, -13.24) * mm, "end": v(15.62, -13.2) * mm});
            skArc(sketch, "E16.47.12", {"start": v(15.52, -13.85) * mm, "mid": v(15.48, -13.88) * mm, "end": v(15.43, -13.89) * mm});
            skArc(sketch, "E16.47.13", {"start": v(15.19, -13.87) * mm, "mid": v(15.13, -13.86) * mm, "end": v(15.07, -13.82) * mm});
            skLineSegment(sketch, "E16.47.14", {"start": v(15.61, -13.74) * mm, "end": v(15.71, -13.63) * mm});
            skPoint(sketch, "E16.48.0", {"position": v(16.74, -11.86) * mm});
            skLineSegment(sketch, "E16.48.1", {"start": v(16.31, -12.53) * mm, "end": v(16.56, -12.53) * mm});
            skPoint(sketch, "E16.48.2", {"position": v(16.24, -12.53) * mm});
            skLineSegment(sketch, "E16.48.3", {"start": v(16.72, -12.37) * mm, "end": v(16.08, -11.9) * mm});
            skLineSegment(sketch, "E16.48.4", {"start": v(16.69, -11.82) * mm, "end": v(16.33, -11.55) * mm});
            skPoint(sketch, "E16.48.5", {"position": v(16.6, -12.53) * mm});
            skLineSegment(sketch, "E16.48.6", {"start": v(16.72, -12.37) * mm, "end": v(16.63, -12.49) * mm});
            skPoint(sketch, "E16.48.7", {"position": v(16.84, -12.2) * mm});
            skLineSegment(sketch, "E16.48.8", {"start": v(16.76, -11.93) * mm, "end": v(16.83, -12.16) * mm});
            skLineSegment(sketch, "E16.48.9", {"start": v(16.19, -12.5) * mm, "end": v(15.83, -12.23) * mm});
            skArc(sketch, "E16.48.10", {"start": v(16.81, -12.25) * mm, "mid": v(16.83, -12.2) * mm, "end": v(16.83, -12.16) * mm});
            skArc(sketch, "E16.48.11", {"start": v(16.76, -11.93) * mm, "mid": v(16.73, -11.87) * mm, "end": v(16.69, -11.82) * mm});
            skArc(sketch, "E16.48.12", {"start": v(16.63, -12.49) * mm, "mid": v(16.6, -12.52) * mm, "end": v(16.56, -12.53) * mm});
            skArc(sketch, "E16.48.13", {"start": v(16.31, -12.53) * mm, "mid": v(16.25, -12.52) * mm, "end": v(16.19, -12.5) * mm});
            skLineSegment(sketch, "E16.48.14", {"start": v(16.72, -12.37) * mm, "end": v(16.81, -12.25) * mm});
            skPoint(sketch, "E16.49.0", {"position": v(17.69, -10.4) * mm});
            skLineSegment(sketch, "E16.49.1", {"start": v(17.31, -11.1) * mm, "end": v(17.56, -11.08) * mm});
            skPoint(sketch, "E16.49.2", {"position": v(17.25, -11.11) * mm});
            skLineSegment(sketch, "E16.49.3", {"start": v(17.71, -10.9) * mm, "end": v(17.03, -10.49) * mm});
            skLineSegment(sketch, "E16.49.4", {"start": v(17.63, -10.36) * mm, "end": v(17.25, -10.13) * mm});
            skPoint(sketch, "E16.49.5", {"position": v(17.6, -11.07) * mm});
            skLineSegment(sketch, "E16.49.6", {"start": v(17.71, -10.9) * mm, "end": v(17.63, -11.03) * mm});
            skPoint(sketch, "E16.49.7", {"position": v(17.82, -10.74) * mm});
            skLineSegment(sketch, "E16.49.8", {"start": v(17.71, -10.46) * mm, "end": v(17.8, -10.7) * mm});
            skLineSegment(sketch, "E16.49.9", {"start": v(17.19, -11.08) * mm, "end": v(16.8, -10.84) * mm});
            skArc(sketch, "E16.49.10", {"start": v(17.8, -10.78) * mm, "mid": v(17.8, -10.74) * mm, "end": v(17.8, -10.7) * mm});
            skArc(sketch, "E16.49.11", {"start": v(17.71, -10.46) * mm, "mid": v(17.68, -10.4) * mm, "end": v(17.63, -10.36) * mm});
            skArc(sketch, "E16.49.12", {"start": v(17.63, -11.03) * mm, "mid": v(17.6, -11.07) * mm, "end": v(17.56, -11.08) * mm});
            skArc(sketch, "E16.49.13", {"start": v(17.31, -11.1) * mm, "mid": v(17.25, -11.1) * mm, "end": v(17.19, -11.08) * mm});
            skLineSegment(sketch, "E16.49.14", {"start": v(17.71, -10.9) * mm, "end": v(17.8, -10.78) * mm});
            skPoint(sketch, "E16.50.0", {"position": v(18.5, -8.86) * mm});
            skLineSegment(sketch, "E16.50.1", {"start": v(18.2, -9.6) * mm, "end": v(18.44, -9.55) * mm});
            skPoint(sketch, "E16.50.2", {"position": v(18.13, -9.6) * mm});
            skLineSegment(sketch, "E16.50.3", {"start": v(18.57, -9.36) * mm, "end": v(17.86, -9) * mm});
            skLineSegment(sketch, "E16.50.4", {"start": v(18.44, -8.83) * mm, "end": v(18.04, -8.63) * mm});
            skPoint(sketch, "E16.50.5", {"position": v(18.48, -9.54) * mm});
            skLineSegment(sketch, "E16.50.6", {"start": v(18.57, -9.36) * mm, "end": v(18.5, -9.5) * mm});
            skPoint(sketch, "E16.50.7", {"position": v(18.66, -9.19) * mm});
            skLineSegment(sketch, "E16.50.8", {"start": v(18.53, -8.92) * mm, "end": v(18.64, -9.14) * mm});
            skLineSegment(sketch, "E16.50.9", {"start": v(18.07, -9.58) * mm, "end": v(17.67, -9.38) * mm});
            skArc(sketch, "E16.50.10", {"start": v(18.64, -9.23) * mm, "mid": v(18.65, -9.19) * mm, "end": v(18.64, -9.14) * mm});
            skArc(sketch, "E16.50.11", {"start": v(18.53, -8.92) * mm, "mid": v(18.5, -8.87) * mm, "end": v(18.44, -8.83) * mm});
            skArc(sketch, "E16.50.12", {"start": v(18.5, -9.5) * mm, "mid": v(18.48, -9.53) * mm, "end": v(18.44, -9.55) * mm});
            skArc(sketch, "E16.50.13", {"start": v(18.2, -9.6) * mm, "mid": v(18.13, -9.6) * mm, "end": v(18.07, -9.58) * mm});
            skLineSegment(sketch, "E16.50.14", {"start": v(18.57, -9.36) * mm, "end": v(18.64, -9.23) * mm});
            skPoint(sketch, "E16.51.0", {"position": v(19.19, -7.26) * mm});
            skLineSegment(sketch, "E16.51.1", {"start": v(18.94, -8.02) * mm, "end": v(19.18, -7.95) * mm});
            skPoint(sketch, "E16.51.2", {"position": v(18.88, -8.04) * mm});
            skLineSegment(sketch, "E16.51.3", {"start": v(19.3, -7.76) * mm, "end": v(18.56, -7.46) * mm});
            skLineSegment(sketch, "E16.51.4", {"start": v(19.13, -7.23) * mm, "end": v(18.71, -7.07) * mm});
            skPoint(sketch, "E16.51.5", {"position": v(19.23, -7.94) * mm});
            skLineSegment(sketch, "E16.51.6", {"start": v(19.3, -7.76) * mm, "end": v(19.25, -7.9) * mm});
            skPoint(sketch, "E16.51.7", {"position": v(19.37, -7.57) * mm});
            skLineSegment(sketch, "E16.51.8", {"start": v(19.22, -7.32) * mm, "end": v(19.35, -7.53) * mm});
            skLineSegment(sketch, "E16.51.9", {"start": v(18.81, -8.01) * mm, "end": v(18.4, -7.84) * mm});
            skArc(sketch, "E16.51.10", {"start": v(19.36, -7.62) * mm, "mid": v(19.36, -7.57) * mm, "end": v(19.35, -7.53) * mm});
            skArc(sketch, "E16.51.11", {"start": v(19.22, -7.32) * mm, "mid": v(19.18, -7.27) * mm, "end": v(19.13, -7.23) * mm});
            skArc(sketch, "E16.51.12", {"start": v(19.25, -7.9) * mm, "mid": v(19.22, -7.93) * mm, "end": v(19.18, -7.95) * mm});
            skArc(sketch, "E16.51.13", {"start": v(18.94, -8.02) * mm, "mid": v(18.88, -8.03) * mm, "end": v(18.81, -8.01) * mm});
            skLineSegment(sketch, "E16.51.14", {"start": v(19.3, -7.76) * mm, "end": v(19.36, -7.62) * mm});
            skPoint(sketch, "E16.52.0", {"position": v(19.74, -5.6) * mm});
            skLineSegment(sketch, "E16.52.1", {"start": v(19.55, -6.38) * mm, "end": v(19.78, -6.3) * mm});
            skPoint(sketch, "E16.52.2", {"position": v(19.5, -6.4) * mm});
            skLineSegment(sketch, "E16.52.3", {"start": v(19.89, -6.1) * mm, "end": v(19.12, -5.86) * mm});
            skLineSegment(sketch, "E16.52.4", {"start": v(19.67, -5.59) * mm, "end": v(19.24, -5.45) * mm});
            skPoint(sketch, "E16.52.5", {"position": v(19.83, -6.28) * mm});
            skLineSegment(sketch, "E16.52.6", {"start": v(19.89, -6.1) * mm, "end": v(19.85, -6.23) * mm});
            skPoint(sketch, "E16.52.7", {"position": v(19.95, -5.9) * mm});
            skLineSegment(sketch, "E16.52.8", {"start": v(19.78, -5.66) * mm, "end": v(19.92, -5.86) * mm});
            skLineSegment(sketch, "E16.52.9", {"start": v(19.43, -6.39) * mm, "end": v(19, -6.26) * mm});
            skArc(sketch, "E16.52.10", {"start": v(19.93, -5.95) * mm, "mid": v(19.94, -5.9) * mm, "end": v(19.92, -5.86) * mm});
            skArc(sketch, "E16.52.11", {"start": v(19.78, -5.66) * mm, "mid": v(19.73, -5.61) * mm, "end": v(19.67, -5.59) * mm});
            skArc(sketch, "E16.52.12", {"start": v(19.85, -6.23) * mm, "mid": v(19.82, -6.27) * mm, "end": v(19.78, -6.3) * mm});
            skArc(sketch, "E16.52.13", {"start": v(19.55, -6.38) * mm, "mid": v(19.5, -6.4) * mm, "end": v(19.43, -6.39) * mm});
            skLineSegment(sketch, "E16.52.14", {"start": v(19.89, -6.1) * mm, "end": v(19.93, -5.95) * mm});
            skPoint(sketch, "E16.53.0", {"position": v(20.14, -3.91) * mm});
            skLineSegment(sketch, "E16.53.1", {"start": v(20.03, -4.7) * mm, "end": v(20.25, -4.6) * mm});
            skPoint(sketch, "E16.53.2", {"position": v(19.96, -4.73) * mm});
            skLineSegment(sketch, "E16.53.3", {"start": v(20.33, -4.38) * mm, "end": v(19.55, -4.21) * mm});
            skLineSegment(sketch, "E16.53.4", {"start": v(20.07, -3.9) * mm, "end": v(19.64, -3.8) * mm});
            skPoint(sketch, "E16.53.5", {"position": v(20.3, -4.58) * mm});
            skLineSegment(sketch, "E16.53.6", {"start": v(20.33, -4.38) * mm, "end": v(20.3, -4.53) * mm});
            skPoint(sketch, "E16.53.7", {"position": v(20.38, -4.19) * mm});
            skLineSegment(sketch, "E16.53.8", {"start": v(20.18, -3.96) * mm, "end": v(20.34, -4.15) * mm});
            skLineSegment(sketch, "E16.53.9", {"start": v(19.9, -4.72) * mm, "end": v(19.46, -4.62) * mm});
            skArc(sketch, "E16.53.10", {"start": v(20.37, -4.24) * mm, "mid": v(20.36, -4.2) * mm, "end": v(20.34, -4.15) * mm});
            skArc(sketch, "E16.53.11", {"start": v(20.18, -3.96) * mm, "mid": v(20.13, -3.92) * mm, "end": v(20.07, -3.9) * mm});
            skArc(sketch, "E16.53.12", {"start": v(20.3, -4.53) * mm, "mid": v(20.28, -4.57) * mm, "end": v(20.25, -4.6) * mm});
            skArc(sketch, "E16.53.13", {"start": v(20.03, -4.7) * mm, "mid": v(19.96, -4.72) * mm, "end": v(19.9, -4.72) * mm});
            skLineSegment(sketch, "E16.53.14", {"start": v(20.33, -4.38) * mm, "end": v(20.37, -4.24) * mm});
            skPoint(sketch, "E16.54.0", {"position": v(20.4, -2.19) * mm});
            skLineSegment(sketch, "E16.54.1", {"start": v(20.35, -2.99) * mm, "end": v(20.56, -2.86) * mm});
            skPoint(sketch, "E16.54.2", {"position": v(20.3, -3.02) * mm});
            skLineSegment(sketch, "E16.54.3", {"start": v(20.63, -2.64) * mm, "end": v(19.84, -2.54) * mm});
            skLineSegment(sketch, "E16.54.4", {"start": v(20.33, -2.18) * mm, "end": v(19.89, -2.12) * mm});
            skPoint(sketch, "E16.54.5", {"position": v(20.6, -2.84) * mm});
            skLineSegment(sketch, "E16.54.6", {"start": v(20.63, -2.64) * mm, "end": v(20.61, -2.79) * mm});
            skPoint(sketch, "E16.54.7", {"position": v(20.66, -2.45) * mm});
            skLineSegment(sketch, "E16.54.8", {"start": v(20.45, -2.24) * mm, "end": v(20.62, -2.41) * mm});
            skLineSegment(sketch, "E16.54.9", {"start": v(20.23, -3.01) * mm, "end": v(19.78, -2.96) * mm});
            skArc(sketch, "E16.54.10", {"start": v(20.65, -2.5) * mm, "mid": v(20.65, -2.45) * mm, "end": v(20.62, -2.41) * mm});
            skArc(sketch, "E16.54.11", {"start": v(20.45, -2.24) * mm, "mid": v(20.4, -2.2) * mm, "end": v(20.33, -2.18) * mm});
            skArc(sketch, "E16.54.12", {"start": v(20.61, -2.79) * mm, "mid": v(20.6, -2.83) * mm, "end": v(20.56, -2.86) * mm});
            skArc(sketch, "E16.54.13", {"start": v(20.35, -2.99) * mm, "mid": v(20.3, -3.01) * mm, "end": v(20.23, -3.01) * mm});
            skLineSegment(sketch, "E16.54.14", {"start": v(20.63, -2.64) * mm, "end": v(20.65, -2.5) * mm});
            skPoint(sketch, "E16.55.0", {"position": v(20.51, -0.45) * mm});
            skLineSegment(sketch, "E16.55.1", {"start": v(20.53, -1.25) * mm, "end": v(20.73, -1.1) * mm});
            skPoint(sketch, "E16.55.2", {"position": v(20.48, -1.29) * mm});
            skLineSegment(sketch, "E16.55.3", {"start": v(20.78, -0.88) * mm, "end": v(19.98, -0.85) * mm});
            skLineSegment(sketch, "E16.55.4", {"start": v(20.44, -0.45) * mm, "end": v(20, -0.43) * mm});
            skPoint(sketch, "E16.55.5", {"position": v(20.77, -1.08) * mm});
            skLineSegment(sketch, "E16.55.6", {"start": v(20.78, -0.88) * mm, "end": v(20.78, -1.03) * mm});
            skPoint(sketch, "E16.55.7", {"position": v(20.8, -0.68) * mm});
            skLineSegment(sketch, "E16.55.8", {"start": v(20.56, -0.5) * mm, "end": v(20.75, -0.65) * mm});
            skLineSegment(sketch, "E16.55.9", {"start": v(20.4, -1.29) * mm, "end": v(19.96, -1.27) * mm});
            skArc(sketch, "E16.55.10", {"start": v(20.79, -0.73) * mm, "mid": v(20.78, -0.69) * mm, "end": v(20.75, -0.65) * mm});
            skArc(sketch, "E16.55.11", {"start": v(20.56, -0.5) * mm, "mid": v(20.5, -0.46) * mm, "end": v(20.44, -0.45) * mm});
            skArc(sketch, "E16.55.12", {"start": v(20.78, -1.03) * mm, "mid": v(20.76, -1.08) * mm, "end": v(20.73, -1.1) * mm});
            skArc(sketch, "E16.55.13", {"start": v(20.53, -1.25) * mm, "mid": v(20.47, -1.28) * mm, "end": v(20.4, -1.29) * mm});
            skLineSegment(sketch, "E16.55.14", {"start": v(20.78, -0.88) * mm, "end": v(20.79, -0.73) * mm});
            skPoint(sketch, "E16.56.0", {"position": v(20.48, 1.29) * mm});
            skLineSegment(sketch, "E16.56.1", {"start": v(20.56, 0.5) * mm, "end": v(20.75, 0.65) * mm});
            skPoint(sketch, "E16.56.2", {"position": v(20.51, 0.45) * mm});
            skLineSegment(sketch, "E16.56.3", {"start": v(20.78, 0.88) * mm, "end": v(19.98, 0.85) * mm});
            skLineSegment(sketch, "E16.56.4", {"start": v(20.4, 1.29) * mm, "end": v(19.96, 1.27) * mm});
            skPoint(sketch, "E16.56.5", {"position": v(20.8, 0.68) * mm});
            skLineSegment(sketch, "E16.56.6", {"start": v(20.78, 0.88) * mm, "end": v(20.79, 0.73) * mm});
            skPoint(sketch, "E16.56.7", {"position": v(20.77, 1.08) * mm});
            skLineSegment(sketch, "E16.56.8", {"start": v(20.53, 1.25) * mm, "end": v(20.73, 1.1) * mm});
            skLineSegment(sketch, "E16.56.9", {"start": v(20.44, 0.45) * mm, "end": v(20, 0.43) * mm});
            skArc(sketch, "E16.56.10", {"start": v(20.78, 1.03) * mm, "mid": v(20.76, 1.08) * mm, "end": v(20.73, 1.1) * mm});
            skArc(sketch, "E16.56.11", {"start": v(20.53, 1.25) * mm, "mid": v(20.47, 1.28) * mm, "end": v(20.4, 1.29) * mm});
            skArc(sketch, "E16.56.12", {"start": v(20.79, 0.73) * mm, "mid": v(20.78, 0.69) * mm, "end": v(20.75, 0.65) * mm});
            skArc(sketch, "E16.56.13", {"start": v(20.56, 0.5) * mm, "mid": v(20.5, 0.46) * mm, "end": v(20.44, 0.45) * mm});
            skLineSegment(sketch, "E16.56.14", {"start": v(20.78, 0.88) * mm, "end": v(20.78, 1.03) * mm});
            skPoint(sketch, "E16.57.0", {"position": v(20.3, 3.02) * mm});
            skLineSegment(sketch, "E16.57.1", {"start": v(20.45, 2.24) * mm, "end": v(20.62, 2.41) * mm});
            skPoint(sketch, "E16.57.2", {"position": v(20.4, 2.19) * mm});
            skLineSegment(sketch, "E16.57.3", {"start": v(20.63, 2.64) * mm, "end": v(19.84, 2.54) * mm});
            skLineSegment(sketch, "E16.57.4", {"start": v(20.23, 3.01) * mm, "end": v(19.78, 2.96) * mm});
            skPoint(sketch, "E16.57.5", {"position": v(20.66, 2.45) * mm});
            skLineSegment(sketch, "E16.57.6", {"start": v(20.63, 2.64) * mm, "end": v(20.65, 2.5) * mm});
            skPoint(sketch, "E16.57.7", {"position": v(20.6, 2.84) * mm});
            skLineSegment(sketch, "E16.57.8", {"start": v(20.35, 2.99) * mm, "end": v(20.56, 2.86) * mm});
            skLineSegment(sketch, "E16.57.9", {"start": v(20.33, 2.18) * mm, "end": v(19.89, 2.12) * mm});
            skArc(sketch, "E16.57.10", {"start": v(20.61, 2.79) * mm, "mid": v(20.6, 2.83) * mm, "end": v(20.56, 2.86) * mm});
            skArc(sketch, "E16.57.11", {"start": v(20.35, 2.99) * mm, "mid": v(20.3, 3.01) * mm, "end": v(20.23, 3.01) * mm});
            skArc(sketch, "E16.57.12", {"start": v(20.65, 2.5) * mm, "mid": v(20.65, 2.45) * mm, "end": v(20.62, 2.41) * mm});
            skArc(sketch, "E16.57.13", {"start": v(20.45, 2.24) * mm, "mid": v(20.4, 2.2) * mm, "end": v(20.33, 2.18) * mm});
            skLineSegment(sketch, "E16.57.14", {"start": v(20.63, 2.64) * mm, "end": v(20.61, 2.79) * mm});
            skPoint(sketch, "E16.58.0", {"position": v(19.96, 4.73) * mm});
            skLineSegment(sketch, "E16.58.1", {"start": v(20.18, 3.96) * mm, "end": v(20.34, 4.15) * mm});
            skPoint(sketch, "E16.58.2", {"position": v(20.14, 3.91) * mm});
            skLineSegment(sketch, "E16.58.3", {"start": v(20.33, 4.38) * mm, "end": v(19.55, 4.21) * mm});
            skLineSegment(sketch, "E16.58.4", {"start": v(19.9, 4.72) * mm, "end": v(19.46, 4.62) * mm});
            skPoint(sketch, "E16.58.5", {"position": v(20.38, 4.19) * mm});
            skLineSegment(sketch, "E16.58.6", {"start": v(20.33, 4.38) * mm, "end": v(20.37, 4.24) * mm});
            skPoint(sketch, "E16.58.7", {"position": v(20.3, 4.58) * mm});
            skLineSegment(sketch, "E16.58.8", {"start": v(20.03, 4.7) * mm, "end": v(20.25, 4.6) * mm});
            skLineSegment(sketch, "E16.58.9", {"start": v(20.07, 3.9) * mm, "end": v(19.64, 3.8) * mm});
            skArc(sketch, "E16.58.10", {"start": v(20.3, 4.53) * mm, "mid": v(20.28, 4.57) * mm, "end": v(20.25, 4.6) * mm});
            skArc(sketch, "E16.58.11", {"start": v(20.03, 4.7) * mm, "mid": v(19.96, 4.72) * mm, "end": v(19.9, 4.72) * mm});
            skArc(sketch, "E16.58.12", {"start": v(20.37, 4.24) * mm, "mid": v(20.36, 4.2) * mm, "end": v(20.34, 4.15) * mm});
            skArc(sketch, "E16.58.13", {"start": v(20.18, 3.96) * mm, "mid": v(20.13, 3.92) * mm, "end": v(20.07, 3.9) * mm});
            skLineSegment(sketch, "E16.58.14", {"start": v(20.33, 4.38) * mm, "end": v(20.3, 4.53) * mm});
            skPoint(sketch, "E16.59.0", {"position": v(19.5, 6.4) * mm});
            skLineSegment(sketch, "E16.59.1", {"start": v(19.78, 5.66) * mm, "end": v(19.92, 5.86) * mm});
            skPoint(sketch, "E16.59.2", {"position": v(19.74, 5.6) * mm});
            skLineSegment(sketch, "E16.59.3", {"start": v(19.89, 6.1) * mm, "end": v(19.12, 5.86) * mm});
            skLineSegment(sketch, "E16.59.4", {"start": v(19.43, 6.39) * mm, "end": v(19, 6.26) * mm});
            skPoint(sketch, "E16.59.5", {"position": v(19.95, 5.9) * mm});
            skLineSegment(sketch, "E16.59.6", {"start": v(19.89, 6.1) * mm, "end": v(19.93, 5.95) * mm});
            skPoint(sketch, "E16.59.7", {"position": v(19.83, 6.28) * mm});
            skLineSegment(sketch, "E16.59.8", {"start": v(19.55, 6.38) * mm, "end": v(19.78, 6.3) * mm});
            skLineSegment(sketch, "E16.59.9", {"start": v(19.67, 5.59) * mm, "end": v(19.24, 5.45) * mm});
            skArc(sketch, "E16.59.10", {"start": v(19.85, 6.23) * mm, "mid": v(19.82, 6.27) * mm, "end": v(19.78, 6.3) * mm});
            skArc(sketch, "E16.59.11", {"start": v(19.55, 6.38) * mm, "mid": v(19.5, 6.4) * mm, "end": v(19.43, 6.39) * mm});
            skArc(sketch, "E16.59.12", {"start": v(19.93, 5.95) * mm, "mid": v(19.94, 5.9) * mm, "end": v(19.92, 5.86) * mm});
            skArc(sketch, "E16.59.13", {"start": v(19.78, 5.66) * mm, "mid": v(19.73, 5.61) * mm, "end": v(19.67, 5.59) * mm});
            skLineSegment(sketch, "E16.59.14", {"start": v(19.89, 6.1) * mm, "end": v(19.85, 6.23) * mm});
            skPoint(sketch, "E16.60.0", {"position": v(18.88, 8.04) * mm});
            skLineSegment(sketch, "E16.60.1", {"start": v(19.22, 7.32) * mm, "end": v(19.35, 7.53) * mm});
            skPoint(sketch, "E16.60.2", {"position": v(19.19, 7.26) * mm});
            skLineSegment(sketch, "E16.60.3", {"start": v(19.3, 7.76) * mm, "end": v(18.56, 7.46) * mm});
            skLineSegment(sketch, "E16.60.4", {"start": v(18.81, 8.01) * mm, "end": v(18.4, 7.84) * mm});
            skPoint(sketch, "E16.60.5", {"position": v(19.37, 7.57) * mm});
            skLineSegment(sketch, "E16.60.6", {"start": v(19.3, 7.76) * mm, "end": v(19.36, 7.62) * mm});
            skPoint(sketch, "E16.60.7", {"position": v(19.23, 7.94) * mm});
            skLineSegment(sketch, "E16.60.8", {"start": v(18.94, 8.02) * mm, "end": v(19.18, 7.95) * mm});
            skLineSegment(sketch, "E16.60.9", {"start": v(19.13, 7.23) * mm, "end": v(18.71, 7.07) * mm});
            skArc(sketch, "E16.60.10", {"start": v(19.25, 7.9) * mm, "mid": v(19.22, 7.93) * mm, "end": v(19.18, 7.95) * mm});
            skArc(sketch, "E16.60.11", {"start": v(18.94, 8.02) * mm, "mid": v(18.88, 8.03) * mm, "end": v(18.81, 8.01) * mm});
            skArc(sketch, "E16.60.12", {"start": v(19.36, 7.62) * mm, "mid": v(19.36, 7.57) * mm, "end": v(19.35, 7.53) * mm});
            skArc(sketch, "E16.60.13", {"start": v(19.22, 7.32) * mm, "mid": v(19.18, 7.27) * mm, "end": v(19.13, 7.23) * mm});
            skLineSegment(sketch, "E16.60.14", {"start": v(19.3, 7.76) * mm, "end": v(19.25, 7.9) * mm});
            skPoint(sketch, "E16.61.0", {"position": v(18.13, 9.6) * mm});
            skLineSegment(sketch, "E16.61.1", {"start": v(18.53, 8.92) * mm, "end": v(18.64, 9.14) * mm});
            skPoint(sketch, "E16.61.2", {"position": v(18.5, 8.86) * mm});
            skLineSegment(sketch, "E16.61.3", {"start": v(18.57, 9.36) * mm, "end": v(17.86, 9) * mm});
            skLineSegment(sketch, "E16.61.4", {"start": v(18.07, 9.58) * mm, "end": v(17.67, 9.38) * mm});
            skPoint(sketch, "E16.61.5", {"position": v(18.66, 9.19) * mm});
            skLineSegment(sketch, "E16.61.6", {"start": v(18.57, 9.36) * mm, "end": v(18.64, 9.23) * mm});
            skPoint(sketch, "E16.61.7", {"position": v(18.48, 9.54) * mm});
            skLineSegment(sketch, "E16.61.8", {"start": v(18.2, 9.6) * mm, "end": v(18.44, 9.55) * mm});
            skLineSegment(sketch, "E16.61.9", {"start": v(18.44, 8.83) * mm, "end": v(18.04, 8.63) * mm});
            skArc(sketch, "E16.61.10", {"start": v(18.5, 9.5) * mm, "mid": v(18.48, 9.53) * mm, "end": v(18.44, 9.55) * mm});
            skArc(sketch, "E16.61.11", {"start": v(18.2, 9.6) * mm, "mid": v(18.13, 9.6) * mm, "end": v(18.07, 9.58) * mm});
            skArc(sketch, "E16.61.12", {"start": v(18.64, 9.23) * mm, "mid": v(18.65, 9.19) * mm, "end": v(18.64, 9.14) * mm});
            skArc(sketch, "E16.61.13", {"start": v(18.53, 8.92) * mm, "mid": v(18.5, 8.87) * mm, "end": v(18.44, 8.83) * mm});
            skLineSegment(sketch, "E16.61.14", {"start": v(18.57, 9.36) * mm, "end": v(18.5, 9.5) * mm});
            skPoint(sketch, "E16.62.0", {"position": v(17.25, 11.11) * mm});
            skLineSegment(sketch, "E16.62.1", {"start": v(17.71, 10.46) * mm, "end": v(17.8, 10.7) * mm});
            skPoint(sketch, "E16.62.2", {"position": v(17.69, 10.4) * mm});
            skLineSegment(sketch, "E16.62.3", {"start": v(17.71, 10.9) * mm, "end": v(17.03, 10.49) * mm});
            skLineSegment(sketch, "E16.62.4", {"start": v(17.19, 11.08) * mm, "end": v(16.8, 10.84) * mm});
            skPoint(sketch, "E16.62.5", {"position": v(17.82, 10.74) * mm});
            skLineSegment(sketch, "E16.62.6", {"start": v(17.71, 10.9) * mm, "end": v(17.8, 10.78) * mm});
            skPoint(sketch, "E16.62.7", {"position": v(17.6, 11.07) * mm});
            skLineSegment(sketch, "E16.62.8", {"start": v(17.31, 11.1) * mm, "end": v(17.56, 11.08) * mm});
            skLineSegment(sketch, "E16.62.9", {"start": v(17.63, 10.36) * mm, "end": v(17.25, 10.13) * mm});
            skArc(sketch, "E16.62.10", {"start": v(17.63, 11.03) * mm, "mid": v(17.6, 11.07) * mm, "end": v(17.56, 11.08) * mm});
            skArc(sketch, "E16.62.11", {"start": v(17.31, 11.1) * mm, "mid": v(17.25, 11.1) * mm, "end": v(17.19, 11.08) * mm});
            skArc(sketch, "E16.62.12", {"start": v(17.8, 10.78) * mm, "mid": v(17.8, 10.74) * mm, "end": v(17.8, 10.7) * mm});
            skArc(sketch, "E16.62.13", {"start": v(17.71, 10.46) * mm, "mid": v(17.68, 10.4) * mm, "end": v(17.63, 10.36) * mm});
            skLineSegment(sketch, "E16.62.14", {"start": v(17.71, 10.9) * mm, "end": v(17.63, 11.03) * mm});
            skPoint(sketch, "E16.63.0", {"position": v(16.24, 12.53) * mm});
            skLineSegment(sketch, "E16.63.1", {"start": v(16.76, 11.93) * mm, "end": v(16.83, 12.16) * mm});
            skPoint(sketch, "E16.63.2", {"position": v(16.74, 11.86) * mm});
            skLineSegment(sketch, "E16.63.3", {"start": v(16.72, 12.37) * mm, "end": v(16.08, 11.9) * mm});
            skLineSegment(sketch, "E16.63.4", {"start": v(16.19, 12.5) * mm, "end": v(15.83, 12.23) * mm});
            skPoint(sketch, "E16.63.5", {"position": v(16.84, 12.2) * mm});
            skLineSegment(sketch, "E16.63.6", {"start": v(16.72, 12.37) * mm, "end": v(16.81, 12.25) * mm});
            skPoint(sketch, "E16.63.7", {"position": v(16.6, 12.53) * mm});
            skLineSegment(sketch, "E16.63.8", {"start": v(16.31, 12.53) * mm, "end": v(16.56, 12.53) * mm});
            skLineSegment(sketch, "E16.63.9", {"start": v(16.69, 11.82) * mm, "end": v(16.33, 11.55) * mm});
            skArc(sketch, "E16.63.10", {"start": v(16.63, 12.49) * mm, "mid": v(16.6, 12.52) * mm, "end": v(16.56, 12.53) * mm});
            skArc(sketch, "E16.63.11", {"start": v(16.31, 12.53) * mm, "mid": v(16.25, 12.52) * mm, "end": v(16.19, 12.5) * mm});
            skArc(sketch, "E16.63.12", {"start": v(16.81, 12.25) * mm, "mid": v(16.83, 12.2) * mm, "end": v(16.83, 12.16) * mm});
            skArc(sketch, "E16.63.13", {"start": v(16.76, 11.93) * mm, "mid": v(16.73, 11.87) * mm, "end": v(16.69, 11.82) * mm});
            skLineSegment(sketch, "E16.63.14", {"start": v(16.72, 12.37) * mm, "end": v(16.63, 12.49) * mm});
            skPoint(sketch, "E16.64.0", {"position": v(15.12, 13.87) * mm});
            skLineSegment(sketch, "E16.64.1", {"start": v(15.69, 13.3) * mm, "end": v(15.74, 13.55) * mm});
            skPoint(sketch, "E16.64.2", {"position": v(15.68, 13.24) * mm});
            skLineSegment(sketch, "E16.64.3", {"start": v(15.61, 13.74) * mm, "end": v(15.01, 13.21) * mm});
            skLineSegment(sketch, "E16.64.4", {"start": v(15.07, 13.82) * mm, "end": v(14.73, 13.53) * mm});
            skPoint(sketch, "E16.64.5", {"position": v(15.75, 13.6) * mm});
            skLineSegment(sketch, "E16.64.6", {"start": v(15.61, 13.74) * mm, "end": v(15.71, 13.63) * mm});
            skPoint(sketch, "E16.64.7", {"position": v(15.48, 13.9) * mm});
            skLineSegment(sketch, "E16.64.8", {"start": v(15.19, 13.87) * mm, "end": v(15.43, 13.89) * mm});
            skLineSegment(sketch, "E16.64.9", {"start": v(15.62, 13.2) * mm, "end": v(15.29, 12.9) * mm});
            skArc(sketch, "E16.64.10", {"start": v(15.52, 13.85) * mm, "mid": v(15.48, 13.88) * mm, "end": v(15.43, 13.89) * mm});
            skArc(sketch, "E16.64.11", {"start": v(15.19, 13.87) * mm, "mid": v(15.13, 13.86) * mm, "end": v(15.07, 13.82) * mm});
            skArc(sketch, "E16.64.12", {"start": v(15.71, 13.63) * mm, "mid": v(15.73, 13.6) * mm, "end": v(15.74, 13.55) * mm});
            skArc(sketch, "E16.64.13", {"start": v(15.69, 13.3) * mm, "mid": v(15.67, 13.24) * mm, "end": v(15.62, 13.2) * mm});
            skLineSegment(sketch, "E16.64.14", {"start": v(15.61, 13.74) * mm, "end": v(15.52, 13.85) * mm});
            skPoint(sketch, "E16.65.0", {"position": v(13.9, 15.1) * mm});
            skLineSegment(sketch, "E16.65.1", {"start": v(14.5, 14.59) * mm, "end": v(14.53, 14.83) * mm});
            skPoint(sketch, "E16.65.2", {"position": v(14.5, 14.52) * mm});
            skLineSegment(sketch, "E16.65.3", {"start": v(14.4, 15.02) * mm, "end": v(13.84, 14.44) * mm});
            skLineSegment(sketch, "E16.65.4", {"start": v(13.84, 15.05) * mm, "end": v(13.53, 14.73) * mm});
            skPoint(sketch, "E16.65.5", {"position": v(14.54, 14.88) * mm});
            skLineSegment(sketch, "E16.65.6", {"start": v(14.4, 15.02) * mm, "end": v(14.5, 14.91) * mm});
            skPoint(sketch, "E16.65.7", {"position": v(14.25, 15.15) * mm});
            skLineSegment(sketch, "E16.65.8", {"start": v(13.96, 15.1) * mm, "end": v(14.2, 15.15) * mm});
            skLineSegment(sketch, "E16.65.9", {"start": v(14.45, 14.47) * mm, "end": v(14.14, 14.15) * mm});
            skArc(sketch, "E16.65.10", {"start": v(14.29, 15.12) * mm, "mid": v(14.25, 15.14) * mm, "end": v(14.2, 15.15) * mm});
            skArc(sketch, "E16.65.11", {"start": v(13.96, 15.1) * mm, "mid": v(13.9, 15.09) * mm, "end": v(13.84, 15.05) * mm});
            skArc(sketch, "E16.65.12", {"start": v(14.5, 14.91) * mm, "mid": v(14.53, 14.88) * mm, "end": v(14.53, 14.83) * mm});
            skArc(sketch, "E16.65.13", {"start": v(14.5, 14.59) * mm, "mid": v(14.49, 14.52) * mm, "end": v(14.45, 14.47) * mm});
            skLineSegment(sketch, "E16.65.14", {"start": v(14.4, 15.02) * mm, "end": v(14.29, 15.12) * mm});
            skPoint(sketch, "E16.66.0", {"position": v(12.56, 16.22) * mm});
            skLineSegment(sketch, "E16.66.1", {"start": v(13.21, 15.76) * mm, "end": v(13.22, 16) * mm});
            skPoint(sketch, "E16.66.2", {"position": v(13.21, 15.7) * mm});
            skLineSegment(sketch, "E16.66.3", {"start": v(13.07, 16.18) * mm, "end": v(12.56, 15.56) * mm});
            skLineSegment(sketch, "E16.66.4", {"start": v(12.52, 16.17) * mm, "end": v(12.24, 15.82) * mm});
            skPoint(sketch, "E16.66.5", {"position": v(13.22, 16.06) * mm});
            skLineSegment(sketch, "E16.66.6", {"start": v(13.07, 16.18) * mm, "end": v(13.18, 16.09) * mm});
            skPoint(sketch, "E16.66.7", {"position": v(12.91, 16.3) * mm});
            skLineSegment(sketch, "E16.66.8", {"start": v(12.63, 16.24) * mm, "end": v(12.87, 16.3) * mm});
            skLineSegment(sketch, "E16.66.9", {"start": v(13.17, 15.64) * mm, "end": v(12.89, 15.3) * mm});
            skArc(sketch, "E16.66.10", {"start": v(12.95, 16.28) * mm, "mid": v(12.91, 16.3) * mm, "end": v(12.87, 16.3) * mm});
            skArc(sketch, "E16.66.11", {"start": v(12.63, 16.24) * mm, "mid": v(12.57, 16.21) * mm, "end": v(12.52, 16.17) * mm});
            skArc(sketch, "E16.66.12", {"start": v(13.18, 16.09) * mm, "mid": v(13.21, 16.05) * mm, "end": v(13.22, 16) * mm});
            skArc(sketch, "E16.66.13", {"start": v(13.21, 15.76) * mm, "mid": v(13.2, 15.7) * mm, "end": v(13.17, 15.64) * mm});
            skLineSegment(sketch, "E16.66.14", {"start": v(13.07, 16.18) * mm, "end": v(12.95, 16.28) * mm});
            skPoint(sketch, "E16.67.0", {"position": v(11.14, 17.23) * mm});
            skLineSegment(sketch, "E16.67.1", {"start": v(11.83, 16.83) * mm, "end": v(11.82, 17.07) * mm});
            skPoint(sketch, "E16.67.2", {"position": v(11.83, 16.76) * mm});
            skLineSegment(sketch, "E16.67.3", {"start": v(11.65, 17.23) * mm, "end": v(11.2, 16.57) * mm});
            skLineSegment(sketch, "E16.67.4", {"start": v(11.1, 17.17) * mm, "end": v(10.85, 16.8) * mm});
            skPoint(sketch, "E16.67.5", {"position": v(11.81, 17.12) * mm});
            skLineSegment(sketch, "E16.67.6", {"start": v(11.65, 17.23) * mm, "end": v(11.77, 17.15) * mm});
            skPoint(sketch, "E16.67.7", {"position": v(11.48, 17.34) * mm});
            skLineSegment(sketch, "E16.67.8", {"start": v(11.2, 17.25) * mm, "end": v(11.44, 17.33) * mm});
            skLineSegment(sketch, "E16.67.9", {"start": v(11.8, 16.7) * mm, "end": v(11.54, 16.33) * mm});
            skArc(sketch, "E16.67.10", {"start": v(11.52, 17.32) * mm, "mid": v(11.48, 17.33) * mm, "end": v(11.44, 17.33) * mm});
            skArc(sketch, "E16.67.11", {"start": v(11.2, 17.25) * mm, "mid": v(11.15, 17.22) * mm, "end": v(11.1, 17.17) * mm});
            skArc(sketch, "E16.67.12", {"start": v(11.77, 17.15) * mm, "mid": v(11.8, 17.12) * mm, "end": v(11.82, 17.07) * mm});
            skArc(sketch, "E16.67.13", {"start": v(11.83, 16.83) * mm, "mid": v(11.82, 16.76) * mm, "end": v(11.8, 16.7) * mm});
            skLineSegment(sketch, "E16.67.14", {"start": v(11.65, 17.23) * mm, "end": v(11.52, 17.32) * mm});
            skPoint(sketch, "E16.68.0", {"position": v(9.64, 18.11) * mm});
            skLineSegment(sketch, "E16.68.1", {"start": v(10.36, 17.77) * mm, "end": v(10.32, 18.01) * mm});
            skPoint(sketch, "E16.68.2", {"position": v(10.37, 17.7) * mm});
            skLineSegment(sketch, "E16.68.3", {"start": v(10.14, 18.16) * mm, "end": v(9.75, 17.46) * mm});
            skLineSegment(sketch, "E16.68.4", {"start": v(9.6, 18.05) * mm, "end": v(9.39, 17.66) * mm});
            skPoint(sketch, "E16.68.5", {"position": v(10.32, 18.06) * mm});
            skLineSegment(sketch, "E16.68.6", {"start": v(10.14, 18.16) * mm, "end": v(10.27, 18.09) * mm});
            skPoint(sketch, "E16.68.7", {"position": v(9.97, 18.26) * mm});
            skLineSegment(sketch, "E16.68.8", {"start": v(9.7, 18.14) * mm, "end": v(9.93, 18.24) * mm});
            skLineSegment(sketch, "E16.68.9", {"start": v(10.34, 17.64) * mm, "end": v(10.12, 17.25) * mm});
            skArc(sketch, "E16.68.10", {"start": v(10.01, 18.23) * mm, "mid": v(9.97, 18.24) * mm, "end": v(9.93, 18.24) * mm});
            skArc(sketch, "E16.68.11", {"start": v(9.7, 18.14) * mm, "mid": v(9.65, 18.1) * mm, "end": v(9.6, 18.05) * mm});
            skArc(sketch, "E16.68.12", {"start": v(10.27, 18.09) * mm, "mid": v(10.3, 18.06) * mm, "end": v(10.32, 18.01) * mm});
            skArc(sketch, "E16.68.13", {"start": v(10.36, 17.77) * mm, "mid": v(10.36, 17.7) * mm, "end": v(10.34, 17.64) * mm});
            skLineSegment(sketch, "E16.68.14", {"start": v(10.14, 18.16) * mm, "end": v(10.01, 18.23) * mm});
            skPoint(sketch, "E16.69.0", {"position": v(8.07, 18.86) * mm});
            skLineSegment(sketch, "E16.69.1", {"start": v(8.82, 18.58) * mm, "end": v(8.76, 18.82) * mm});
            skPoint(sketch, "E16.69.2", {"position": v(8.83, 18.52) * mm});
            skLineSegment(sketch, "E16.69.3", {"start": v(8.57, 18.95) * mm, "end": v(8.24, 18.23) * mm});
            skLineSegment(sketch, "E16.69.4", {"start": v(8.04, 18.8) * mm, "end": v(7.85, 18.4) * mm});
            skPoint(sketch, "E16.69.5", {"position": v(8.75, 18.87) * mm});
            skLineSegment(sketch, "E16.69.6", {"start": v(8.57, 18.95) * mm, "end": v(8.7, 18.9) * mm});
            skPoint(sketch, "E16.69.7", {"position": v(8.39, 19.04) * mm});
            skLineSegment(sketch, "E16.69.8", {"start": v(8.13, 18.9) * mm, "end": v(8.34, 19.01) * mm});
            skLineSegment(sketch, "E16.69.9", {"start": v(8.8, 18.46) * mm, "end": v(8.62, 18.05) * mm});
            skArc(sketch, "E16.69.10", {"start": v(8.43, 19.02) * mm, "mid": v(8.39, 19.02) * mm, "end": v(8.34, 19.01) * mm});
            skArc(sketch, "E16.69.11", {"start": v(8.13, 18.9) * mm, "mid": v(8.08, 18.86) * mm, "end": v(8.04, 18.8) * mm});
            skArc(sketch, "E16.69.12", {"start": v(8.7, 18.9) * mm, "mid": v(8.74, 18.87) * mm, "end": v(8.76, 18.82) * mm});
            skArc(sketch, "E16.69.13", {"start": v(8.82, 18.58) * mm, "mid": v(8.82, 18.52) * mm, "end": v(8.8, 18.46) * mm});
            skLineSegment(sketch, "E16.69.14", {"start": v(8.57, 18.95) * mm, "end": v(8.43, 19.02) * mm});
            skPoint(sketch, "E16.70.0", {"position": v(6.44, 19.48) * mm});
            skLineSegment(sketch, "E16.70.1", {"start": v(7.2, 19.27) * mm, "end": v(7.13, 19.5) * mm});
            skPoint(sketch, "E16.70.2", {"position": v(7.23, 19.2) * mm});
            skLineSegment(sketch, "E16.70.3", {"start": v(6.93, 19.61) * mm, "end": v(6.66, 18.86) * mm});
            skLineSegment(sketch, "E16.70.4", {"start": v(6.42, 19.42) * mm, "end": v(6.27, 19) * mm});
            skPoint(sketch, "E16.70.5", {"position": v(7.12, 19.55) * mm});
            skLineSegment(sketch, "E16.70.6", {"start": v(6.93, 19.61) * mm, "end": v(7.07, 19.56) * mm});
            skPoint(sketch, "E16.70.7", {"position": v(6.74, 19.68) * mm});
            skLineSegment(sketch, "E16.70.8", {"start": v(6.5, 19.52) * mm, "end": v(6.7, 19.65) * mm});
            skLineSegment(sketch, "E16.70.9", {"start": v(7.2, 19.14) * mm, "end": v(7.06, 18.71) * mm});
            skArc(sketch, "E16.70.10", {"start": v(6.79, 19.66) * mm, "mid": v(6.74, 19.67) * mm, "end": v(6.7, 19.65) * mm});
            skArc(sketch, "E16.70.11", {"start": v(6.5, 19.52) * mm, "mid": v(6.45, 19.47) * mm, "end": v(6.42, 19.42) * mm});
            skArc(sketch, "E16.70.12", {"start": v(7.07, 19.56) * mm, "mid": v(7.1, 19.54) * mm, "end": v(7.13, 19.5) * mm});
            skArc(sketch, "E16.70.13", {"start": v(7.2, 19.27) * mm, "mid": v(7.22, 19.2) * mm, "end": v(7.2, 19.14) * mm});
            skLineSegment(sketch, "E16.70.14", {"start": v(6.93, 19.61) * mm, "end": v(6.79, 19.66) * mm});
            skPoint(sketch, "E16.71.0", {"position": v(4.76, 19.96) * mm});
            skLineSegment(sketch, "E16.71.1", {"start": v(5.55, 19.8) * mm, "end": v(5.45, 20.03) * mm});
            skPoint(sketch, "E16.71.2", {"position": v(5.57, 19.75) * mm});
            skLineSegment(sketch, "E16.71.3", {"start": v(5.24, 20.13) * mm, "end": v(5.04, 19.36) * mm});
            skLineSegment(sketch, "E16.71.4", {"start": v(4.75, 19.9) * mm, "end": v(4.63, 19.46) * mm});
            skPoint(sketch, "E16.71.5", {"position": v(5.43, 20.08) * mm});
            skLineSegment(sketch, "E16.71.6", {"start": v(5.24, 20.13) * mm, "end": v(5.39, 20.1) * mm});
            skPoint(sketch, "E16.71.7", {"position": v(5.05, 20.18) * mm});
            skLineSegment(sketch, "E16.71.8", {"start": v(4.82, 20) * mm, "end": v(5.01, 20.15) * mm});
            skLineSegment(sketch, "E16.71.9", {"start": v(5.56, 19.68) * mm, "end": v(5.44, 19.24) * mm});
            skArc(sketch, "E16.71.10", {"start": v(5.1, 20.17) * mm, "mid": v(5.05, 20.17) * mm, "end": v(5.01, 20.15) * mm});
            skArc(sketch, "E16.71.11", {"start": v(4.82, 20) * mm, "mid": v(4.77, 19.95) * mm, "end": v(4.75, 19.9) * mm});
            skArc(sketch, "E16.71.12", {"start": v(5.39, 20.1) * mm, "mid": v(5.43, 20.07) * mm, "end": v(5.45, 20.03) * mm});
            skArc(sketch, "E16.71.13", {"start": v(5.55, 19.8) * mm, "mid": v(5.56, 19.74) * mm, "end": v(5.56, 19.68) * mm});
            skLineSegment(sketch, "E16.71.14", {"start": v(5.24, 20.13) * mm, "end": v(5.1, 20.17) * mm});
            skPoint(sketch, "E16.72.0", {"position": v(3.05, 20.29) * mm});
            skLineSegment(sketch, "E16.72.1", {"start": v(3.85, 20.2) * mm, "end": v(3.73, 20.42) * mm});
            skPoint(sketch, "E16.72.2", {"position": v(3.88, 20.15) * mm});
            skLineSegment(sketch, "E16.72.3", {"start": v(3.52, 20.5) * mm, "end": v(3.38, 19.71) * mm});
            skLineSegment(sketch, "E16.72.4", {"start": v(3.04, 20.22) * mm, "end": v(2.97, 19.78) * mm});
            skPoint(sketch, "E16.72.5", {"position": v(3.71, 20.47) * mm});
            skLineSegment(sketch, "E16.72.6", {"start": v(3.52, 20.5) * mm, "end": v(3.66, 20.48) * mm});
            skPoint(sketch, "E16.72.7", {"position": v(3.32, 20.53) * mm});
            skLineSegment(sketch, "E16.72.8", {"start": v(3.1, 20.33) * mm, "end": v(3.28, 20.5) * mm});
            skLineSegment(sketch, "E16.72.9", {"start": v(3.87, 20.08) * mm, "end": v(3.8, 19.64) * mm});
            skArc(sketch, "E16.72.10", {"start": v(3.37, 20.53) * mm, "mid": v(3.32, 20.52) * mm, "end": v(3.28, 20.5) * mm});
            skArc(sketch, "E16.72.11", {"start": v(3.1, 20.33) * mm, "mid": v(3.06, 20.28) * mm, "end": v(3.04, 20.22) * mm});
            skArc(sketch, "E16.72.12", {"start": v(3.66, 20.48) * mm, "mid": v(3.7, 20.46) * mm, "end": v(3.73, 20.42) * mm});
            skArc(sketch, "E16.72.13", {"start": v(3.85, 20.2) * mm, "mid": v(3.87, 20.14) * mm, "end": v(3.87, 20.08) * mm});
            skLineSegment(sketch, "E16.72.14", {"start": v(3.52, 20.5) * mm, "end": v(3.37, 20.53) * mm});
            skPoint(sketch, "E16.73.0", {"position": v(1.32, 20.47) * mm});
            skLineSegment(sketch, "E16.73.1", {"start": v(2.12, 20.46) * mm, "end": v(1.99, 20.67) * mm});
            skPoint(sketch, "E16.73.2", {"position": v(2.16, 20.4) * mm});
            skLineSegment(sketch, "E16.73.3", {"start": v(1.76, 20.73) * mm, "end": v(1.7, 19.93) * mm});
            skLineSegment(sketch, "E16.73.4", {"start": v(1.32, 20.4) * mm, "end": v(1.28, 19.96) * mm});
            skPoint(sketch, "E16.73.5", {"position": v(1.96, 20.7) * mm});
            skLineSegment(sketch, "E16.73.6", {"start": v(1.76, 20.73) * mm, "end": v(1.91, 20.71) * mm});
            skPoint(sketch, "E16.73.7", {"position": v(1.57, 20.74) * mm});
            skLineSegment(sketch, "E16.73.8", {"start": v(1.37, 20.52) * mm, "end": v(1.53, 20.7) * mm});
            skLineSegment(sketch, "E16.73.9", {"start": v(2.15, 20.34) * mm, "end": v(2.11, 19.89) * mm});
            skArc(sketch, "E16.73.10", {"start": v(1.62, 20.74) * mm, "mid": v(1.57, 20.73) * mm, "end": v(1.53, 20.7) * mm});
            skArc(sketch, "E16.73.11", {"start": v(1.37, 20.52) * mm, "mid": v(1.33, 20.47) * mm, "end": v(1.32, 20.4) * mm});
            skArc(sketch, "E16.73.12", {"start": v(1.91, 20.71) * mm, "mid": v(1.96, 20.7) * mm, "end": v(1.99, 20.67) * mm});
            skArc(sketch, "E16.73.13", {"start": v(2.12, 20.46) * mm, "mid": v(2.15, 20.4) * mm, "end": v(2.15, 20.34) * mm});
            skLineSegment(sketch, "E16.73.14", {"start": v(1.76, 20.73) * mm, "end": v(1.62, 20.74) * mm});
            skSolve(sketch);
        }
        {
            var Q0;
            Q0 = qSketchRegion(id + "F0", true);
            extrude(context, id + "F1", {"entities" : qUnion([Q0]), "endBound" : BoundingType.SYMMETRIC, "depth" : 5 * mm});
        }
    });
